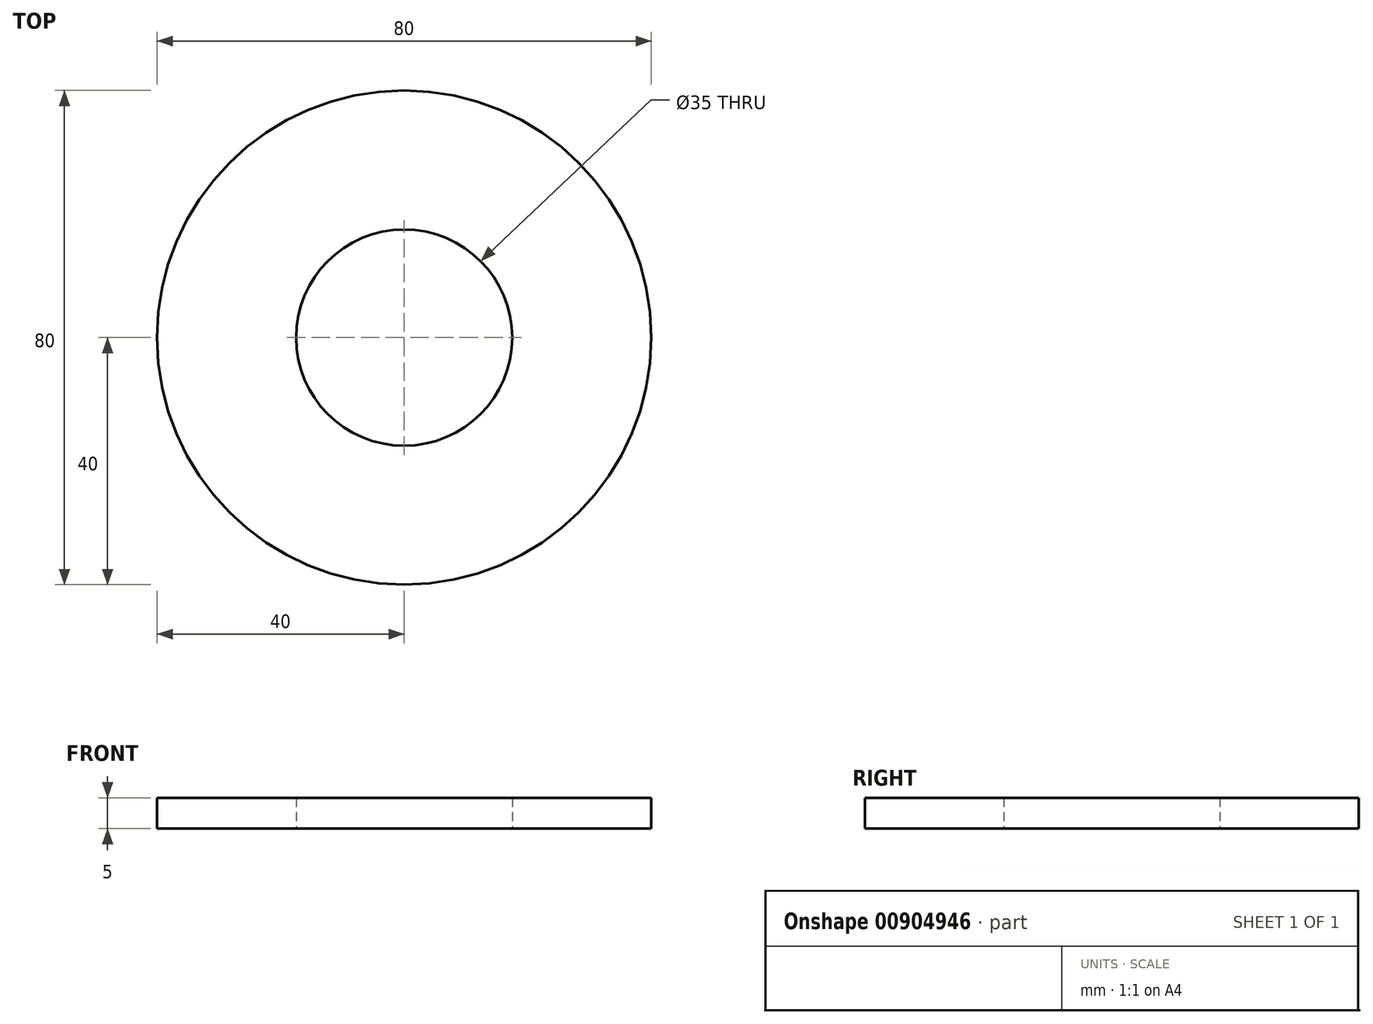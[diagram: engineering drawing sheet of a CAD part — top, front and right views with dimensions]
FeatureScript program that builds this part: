
annotation { "Feature Type Name" : "Feature", "Feature Type Description" : "" }
export const myFeature = defineFeature(function(context is Context, id is Id, definition is map)
    precondition{}
    {
        {
            var Q0;
            Q0=qCreatedBy(makeId("Top.planeOp"),FACE);
            var sketch = newSketch(context, id + "F0", { "sketchPlane" : qUnion([Q0])});
            skArc(sketch, "E0", {"start": v(9.54, 136.41) * mm, "mid": v(4.77, 136.66) * mm, "end": v(0, 136.75) * mm});
            skArc(sketch, "E1", {"start": v(8, 114.55) * mm, "mid": v(4, 114.76) * mm, "end": v(0, 114.83) * mm});
            skLineSegment(sketch, "E2", {"start": v(0, 0) * mm, "end": v(0, 38.61) * mm, "construction": true});
            skLineSegment(sketch, "E3", {"start": v(0, 10) * mm, "end": v(0, 0) * mm, "construction": true});
            skLineSegment(sketch, "E4", {"start": v(0, 0) * mm, "end": v(-47.77, 0) * mm, "construction": true});
            skLineSegment(sketch, "E5", {"start": v(0, 114.83) * mm, "end": v(0, 136.75) * mm});
            skLineSegment(sketch, "E6", {"start": v(8, 114.55) * mm, "end": v(9.54, 136.41) * mm});
            skArc(sketch, "E7.1.0", {"start": v(-10, 114.4) * mm, "mid": v(-14, 113.98) * mm, "end": v(-17.96, 113.42) * mm});
            skLineSegment(sketch, "E7.1.1", {"start": v(-17.96, 113.42) * mm, "end": v(-21.4, 135.06) * mm});
            skArc(sketch, "E7.1.2", {"start": v(-11.92, 136.23) * mm, "mid": v(-16.67, 135.73) * mm, "end": v(-21.4, 135.06) * mm});
            skLineSegment(sketch, "E7.1.3", {"start": v(-10, 114.4) * mm, "end": v(-11.92, 136.23) * mm});
            skArc(sketch, "E7.2.0", {"start": v(-27.78, 111.42) * mm, "mid": v(-31.65, 110.39) * mm, "end": v(-35.49, 109.21) * mm});
            skLineSegment(sketch, "E7.2.1", {"start": v(-35.49, 109.21) * mm, "end": v(-42.26, 130.05) * mm});
            skArc(sketch, "E7.2.2", {"start": v(-33.08, 132.68) * mm, "mid": v(-37.7, 131.45) * mm, "end": v(-42.26, 130.05) * mm});
            skLineSegment(sketch, "E7.2.3", {"start": v(-27.78, 111.42) * mm, "end": v(-33.08, 132.68) * mm});
            skArc(sketch, "E7.3.0", {"start": v(-44.87, 105.7) * mm, "mid": v(-48.53, 104.07) * mm, "end": v(-52.13, 102.32) * mm});
            skLineSegment(sketch, "E7.3.1", {"start": v(-52.13, 102.32) * mm, "end": v(-62.08, 121.84) * mm});
            skArc(sketch, "E7.3.2", {"start": v(-53.43, 125.88) * mm, "mid": v(-57.8, 123.93) * mm, "end": v(-62.08, 121.84) * mm});
            skLineSegment(sketch, "E7.3.3", {"start": v(-44.87, 105.7) * mm, "end": v(-53.43, 125.88) * mm});
            skArc(sketch, "E7.4.0", {"start": v(-60.85, 97.38) * mm, "mid": v(-64.21, 95.2) * mm, "end": v(-67.5, 92.9) * mm});
            skLineSegment(sketch, "E7.4.1", {"start": v(-67.5, 92.9) * mm, "end": v(-80.38, 110.63) * mm});
            skArc(sketch, "E7.4.2", {"start": v(-72.47, 115.97) * mm, "mid": v(-76.47, 113.37) * mm, "end": v(-80.38, 110.63) * mm});
            skLineSegment(sketch, "E7.4.3", {"start": v(-60.85, 97.38) * mm, "end": v(-72.47, 115.97) * mm});
            skArc(sketch, "E7.5.0", {"start": v(-75.34, 86.67) * mm, "mid": v(-78.32, 83.98) * mm, "end": v(-81.2, 81.2) * mm});
            skLineSegment(sketch, "E7.5.1", {"start": v(-81.2, 81.2) * mm, "end": v(-96.7, 96.7) * mm});
            skArc(sketch, "E7.5.2", {"start": v(-89.71, 103.2) * mm, "mid": v(-93.26, 100.01) * mm, "end": v(-96.7, 96.7) * mm});
            skLineSegment(sketch, "E7.5.3", {"start": v(-75.34, 86.67) * mm, "end": v(-89.71, 103.2) * mm});
            skArc(sketch, "E7.6.0", {"start": v(-87.97, 73.81) * mm, "mid": v(-90.5, 70.7) * mm, "end": v(-92.9, 67.5) * mm});
            skLineSegment(sketch, "E7.6.1", {"start": v(-92.9, 67.5) * mm, "end": v(-110.63, 80.38) * mm});
            skArc(sketch, "E7.6.2", {"start": v(-104.75, 87.9) * mm, "mid": v(-107.76, 84.19) * mm, "end": v(-110.63, 80.38) * mm});
            skLineSegment(sketch, "E7.6.3", {"start": v(-87.97, 73.81) * mm, "end": v(-104.75, 87.9) * mm});
            skArc(sketch, "E7.7.0", {"start": v(-98.43, 59.14) * mm, "mid": v(-100.44, 55.67) * mm, "end": v(-102.32, 52.13) * mm});
            skLineSegment(sketch, "E7.7.1", {"start": v(-102.32, 52.13) * mm, "end": v(-121.84, 62.08) * mm});
            skArc(sketch, "E7.7.2", {"start": v(-117.22, 70.43) * mm, "mid": v(-119.6, 66.3) * mm, "end": v(-121.84, 62.08) * mm});
            skLineSegment(sketch, "E7.7.3", {"start": v(-98.43, 59.14) * mm, "end": v(-117.22, 70.43) * mm});
            skArc(sketch, "E7.8.0", {"start": v(-106.47, 43.02) * mm, "mid": v(-107.9, 39.28) * mm, "end": v(-109.21, 35.49) * mm});
            skLineSegment(sketch, "E7.8.1", {"start": v(-109.21, 35.49) * mm, "end": v(-130.05, 42.26) * mm});
            skArc(sketch, "E7.8.2", {"start": v(-126.79, 51.23) * mm, "mid": v(-128.5, 46.77) * mm, "end": v(-130.05, 42.26) * mm});
            skLineSegment(sketch, "E7.8.3", {"start": v(-106.47, 43.02) * mm, "end": v(-126.79, 51.23) * mm});
            skArc(sketch, "E7.9.0", {"start": v(-111.9, 25.83) * mm, "mid": v(-112.72, 21.91) * mm, "end": v(-113.42, 17.96) * mm});
            skLineSegment(sketch, "E7.9.1", {"start": v(-113.42, 17.96) * mm, "end": v(-135.06, 21.4) * mm});
            skArc(sketch, "E7.9.2", {"start": v(-133.24, 30.76) * mm, "mid": v(-134.23, 26.1) * mm, "end": v(-135.06, 21.4) * mm});
            skLineSegment(sketch, "E7.9.3", {"start": v(-111.9, 25.83) * mm, "end": v(-133.24, 30.76) * mm});
            skArc(sketch, "E7.10.0", {"start": v(-114.55, 8) * mm, "mid": v(-114.76, 4) * mm, "end": v(-114.83, 0) * mm});
            skLineSegment(sketch, "E7.10.1", {"start": v(-114.83, 0) * mm, "end": v(-136.75, 0) * mm});
            skArc(sketch, "E7.10.2", {"start": v(-136.41, 9.54) * mm, "mid": v(-136.66, 4.77) * mm, "end": v(-136.75, 0) * mm});
            skLineSegment(sketch, "E7.10.3", {"start": v(-114.55, 8) * mm, "end": v(-136.41, 9.54) * mm});
            skArc(sketch, "E7.11.0", {"start": v(-114.4, -10) * mm, "mid": v(-113.98, -14) * mm, "end": v(-113.42, -17.96) * mm});
            skLineSegment(sketch, "E7.11.1", {"start": v(-113.42, -17.96) * mm, "end": v(-135.06, -21.4) * mm});
            skArc(sketch, "E7.11.2", {"start": v(-136.23, -11.92) * mm, "mid": v(-135.73, -16.67) * mm, "end": v(-135.06, -21.4) * mm});
            skLineSegment(sketch, "E7.11.3", {"start": v(-114.4, -10) * mm, "end": v(-136.23, -11.92) * mm});
            skArc(sketch, "E7.12.0", {"start": v(-111.42, -27.78) * mm, "mid": v(-110.39, -31.65) * mm, "end": v(-109.21, -35.49) * mm});
            skLineSegment(sketch, "E7.12.1", {"start": v(-109.21, -35.49) * mm, "end": v(-130.05, -42.26) * mm});
            skArc(sketch, "E7.12.2", {"start": v(-132.68, -33.08) * mm, "mid": v(-131.45, -37.7) * mm, "end": v(-130.05, -42.26) * mm});
            skLineSegment(sketch, "E7.12.3", {"start": v(-111.42, -27.78) * mm, "end": v(-132.68, -33.08) * mm});
            skArc(sketch, "E7.13.0", {"start": v(-105.7, -44.87) * mm, "mid": v(-104.07, -48.53) * mm, "end": v(-102.32, -52.13) * mm});
            skLineSegment(sketch, "E7.13.1", {"start": v(-102.32, -52.13) * mm, "end": v(-121.84, -62.08) * mm});
            skArc(sketch, "E7.13.2", {"start": v(-125.88, -53.43) * mm, "mid": v(-123.93, -57.8) * mm, "end": v(-121.84, -62.08) * mm});
            skLineSegment(sketch, "E7.13.3", {"start": v(-105.7, -44.87) * mm, "end": v(-125.88, -53.43) * mm});
            skArc(sketch, "E7.14.0", {"start": v(-97.38, -60.85) * mm, "mid": v(-95.2, -64.21) * mm, "end": v(-92.9, -67.5) * mm});
            skLineSegment(sketch, "E7.14.1", {"start": v(-92.9, -67.5) * mm, "end": v(-110.63, -80.38) * mm});
            skArc(sketch, "E7.14.2", {"start": v(-115.97, -72.47) * mm, "mid": v(-113.37, -76.47) * mm, "end": v(-110.63, -80.38) * mm});
            skLineSegment(sketch, "E7.14.3", {"start": v(-97.38, -60.85) * mm, "end": v(-115.97, -72.47) * mm});
            skArc(sketch, "E7.15.0", {"start": v(-86.67, -75.34) * mm, "mid": v(-83.98, -78.32) * mm, "end": v(-81.2, -81.2) * mm});
            skLineSegment(sketch, "E7.15.1", {"start": v(-81.2, -81.2) * mm, "end": v(-96.7, -96.7) * mm});
            skArc(sketch, "E7.15.2", {"start": v(-103.2, -89.71) * mm, "mid": v(-100.01, -93.26) * mm, "end": v(-96.7, -96.7) * mm});
            skLineSegment(sketch, "E7.15.3", {"start": v(-86.67, -75.34) * mm, "end": v(-103.2, -89.71) * mm});
            skArc(sketch, "E7.16.0", {"start": v(-73.81, -87.97) * mm, "mid": v(-70.7, -90.5) * mm, "end": v(-67.5, -92.9) * mm});
            skLineSegment(sketch, "E7.16.1", {"start": v(-67.5, -92.9) * mm, "end": v(-80.38, -110.63) * mm});
            skArc(sketch, "E7.16.2", {"start": v(-87.9, -104.75) * mm, "mid": v(-84.19, -107.76) * mm, "end": v(-80.38, -110.63) * mm});
            skLineSegment(sketch, "E7.16.3", {"start": v(-73.81, -87.97) * mm, "end": v(-87.9, -104.75) * mm});
            skArc(sketch, "E7.17.0", {"start": v(-59.14, -98.43) * mm, "mid": v(-55.67, -100.44) * mm, "end": v(-52.13, -102.32) * mm});
            skLineSegment(sketch, "E7.17.1", {"start": v(-52.13, -102.32) * mm, "end": v(-62.08, -121.84) * mm});
            skArc(sketch, "E7.17.2", {"start": v(-70.43, -117.22) * mm, "mid": v(-66.3, -119.6) * mm, "end": v(-62.08, -121.84) * mm});
            skLineSegment(sketch, "E7.17.3", {"start": v(-59.14, -98.43) * mm, "end": v(-70.43, -117.22) * mm});
            skArc(sketch, "E7.18.0", {"start": v(-43.02, -106.47) * mm, "mid": v(-39.28, -107.9) * mm, "end": v(-35.49, -109.21) * mm});
            skLineSegment(sketch, "E7.18.1", {"start": v(-35.49, -109.21) * mm, "end": v(-42.26, -130.05) * mm});
            skArc(sketch, "E7.18.2", {"start": v(-51.23, -126.79) * mm, "mid": v(-46.77, -128.5) * mm, "end": v(-42.26, -130.05) * mm});
            skLineSegment(sketch, "E7.18.3", {"start": v(-43.02, -106.47) * mm, "end": v(-51.23, -126.79) * mm});
            skArc(sketch, "E7.19.0", {"start": v(-25.83, -111.9) * mm, "mid": v(-21.91, -112.72) * mm, "end": v(-17.96, -113.42) * mm});
            skLineSegment(sketch, "E7.19.1", {"start": v(-17.96, -113.42) * mm, "end": v(-21.4, -135.06) * mm});
            skArc(sketch, "E7.19.2", {"start": v(-30.76, -133.24) * mm, "mid": v(-26.1, -134.23) * mm, "end": v(-21.4, -135.06) * mm});
            skLineSegment(sketch, "E7.19.3", {"start": v(-25.83, -111.9) * mm, "end": v(-30.76, -133.24) * mm});
            skArc(sketch, "E7.20.0", {"start": v(-8, -114.55) * mm, "mid": v(-4, -114.76) * mm, "end": v(0, -114.83) * mm});
            skLineSegment(sketch, "E7.20.1", {"start": v(0, -114.83) * mm, "end": v(0, -136.75) * mm});
            skArc(sketch, "E7.20.2", {"start": v(-9.54, -136.41) * mm, "mid": v(-4.77, -136.66) * mm, "end": v(0, -136.75) * mm});
            skLineSegment(sketch, "E7.20.3", {"start": v(-8, -114.55) * mm, "end": v(-9.54, -136.41) * mm});
            skArc(sketch, "E7.21.0", {"start": v(10, -114.4) * mm, "mid": v(14, -113.98) * mm, "end": v(17.96, -113.42) * mm});
            skLineSegment(sketch, "E7.21.1", {"start": v(17.96, -113.42) * mm, "end": v(21.4, -135.06) * mm});
            skArc(sketch, "E7.21.2", {"start": v(11.92, -136.23) * mm, "mid": v(16.67, -135.73) * mm, "end": v(21.4, -135.06) * mm});
            skLineSegment(sketch, "E7.21.3", {"start": v(10, -114.4) * mm, "end": v(11.92, -136.23) * mm});
            skArc(sketch, "E7.22.0", {"start": v(27.78, -111.42) * mm, "mid": v(31.65, -110.39) * mm, "end": v(35.49, -109.21) * mm});
            skLineSegment(sketch, "E7.22.1", {"start": v(35.49, -109.21) * mm, "end": v(42.26, -130.05) * mm});
            skArc(sketch, "E7.22.2", {"start": v(33.08, -132.68) * mm, "mid": v(37.7, -131.45) * mm, "end": v(42.26, -130.05) * mm});
            skLineSegment(sketch, "E7.22.3", {"start": v(27.78, -111.42) * mm, "end": v(33.08, -132.68) * mm});
            skArc(sketch, "E7.23.0", {"start": v(44.87, -105.7) * mm, "mid": v(48.53, -104.07) * mm, "end": v(52.13, -102.32) * mm});
            skLineSegment(sketch, "E7.23.1", {"start": v(52.13, -102.32) * mm, "end": v(62.08, -121.84) * mm});
            skArc(sketch, "E7.23.2", {"start": v(53.43, -125.88) * mm, "mid": v(57.8, -123.93) * mm, "end": v(62.08, -121.84) * mm});
            skLineSegment(sketch, "E7.23.3", {"start": v(44.87, -105.7) * mm, "end": v(53.43, -125.88) * mm});
            skArc(sketch, "E7.24.0", {"start": v(60.85, -97.38) * mm, "mid": v(64.21, -95.2) * mm, "end": v(67.5, -92.9) * mm});
            skLineSegment(sketch, "E7.24.1", {"start": v(67.5, -92.9) * mm, "end": v(80.38, -110.63) * mm});
            skArc(sketch, "E7.24.2", {"start": v(72.47, -115.97) * mm, "mid": v(76.47, -113.37) * mm, "end": v(80.38, -110.63) * mm});
            skLineSegment(sketch, "E7.24.3", {"start": v(60.85, -97.38) * mm, "end": v(72.47, -115.97) * mm});
            skArc(sketch, "E7.25.0", {"start": v(75.34, -86.67) * mm, "mid": v(78.32, -83.98) * mm, "end": v(81.2, -81.2) * mm});
            skLineSegment(sketch, "E7.25.1", {"start": v(81.2, -81.2) * mm, "end": v(96.7, -96.7) * mm});
            skArc(sketch, "E7.25.2", {"start": v(89.71, -103.2) * mm, "mid": v(93.26, -100.01) * mm, "end": v(96.7, -96.7) * mm});
            skLineSegment(sketch, "E7.25.3", {"start": v(75.34, -86.67) * mm, "end": v(89.71, -103.2) * mm});
            skArc(sketch, "E7.26.0", {"start": v(87.97, -73.81) * mm, "mid": v(90.5, -70.7) * mm, "end": v(92.9, -67.5) * mm});
            skLineSegment(sketch, "E7.26.1", {"start": v(92.9, -67.5) * mm, "end": v(110.63, -80.38) * mm});
            skArc(sketch, "E7.26.2", {"start": v(104.75, -87.9) * mm, "mid": v(107.76, -84.19) * mm, "end": v(110.63, -80.38) * mm});
            skLineSegment(sketch, "E7.26.3", {"start": v(87.97, -73.81) * mm, "end": v(104.75, -87.9) * mm});
            skArc(sketch, "E7.27.0", {"start": v(98.43, -59.14) * mm, "mid": v(100.44, -55.67) * mm, "end": v(102.32, -52.13) * mm});
            skLineSegment(sketch, "E7.27.1", {"start": v(102.32, -52.13) * mm, "end": v(121.84, -62.08) * mm});
            skArc(sketch, "E7.27.2", {"start": v(117.22, -70.43) * mm, "mid": v(119.6, -66.3) * mm, "end": v(121.84, -62.08) * mm});
            skLineSegment(sketch, "E7.27.3", {"start": v(98.43, -59.14) * mm, "end": v(117.22, -70.43) * mm});
            skArc(sketch, "E7.28.0", {"start": v(106.47, -43.02) * mm, "mid": v(107.9, -39.28) * mm, "end": v(109.21, -35.49) * mm});
            skLineSegment(sketch, "E7.28.1", {"start": v(109.21, -35.49) * mm, "end": v(130.05, -42.26) * mm});
            skArc(sketch, "E7.28.2", {"start": v(126.79, -51.23) * mm, "mid": v(128.5, -46.77) * mm, "end": v(130.05, -42.26) * mm});
            skLineSegment(sketch, "E7.28.3", {"start": v(106.47, -43.02) * mm, "end": v(126.79, -51.23) * mm});
            skArc(sketch, "E7.29.0", {"start": v(111.9, -25.83) * mm, "mid": v(112.72, -21.91) * mm, "end": v(113.42, -17.96) * mm});
            skLineSegment(sketch, "E7.29.1", {"start": v(113.42, -17.96) * mm, "end": v(135.06, -21.4) * mm});
            skArc(sketch, "E7.29.2", {"start": v(133.24, -30.76) * mm, "mid": v(134.23, -26.1) * mm, "end": v(135.06, -21.4) * mm});
            skLineSegment(sketch, "E7.29.3", {"start": v(111.9, -25.83) * mm, "end": v(133.24, -30.76) * mm});
            skArc(sketch, "E7.30.0", {"start": v(114.55, -8) * mm, "mid": v(114.76, -4) * mm, "end": v(114.83, 0) * mm});
            skLineSegment(sketch, "E7.30.1", {"start": v(114.83, 0) * mm, "end": v(136.75, 0) * mm});
            skArc(sketch, "E7.30.2", {"start": v(136.41, -9.54) * mm, "mid": v(136.66, -4.77) * mm, "end": v(136.75, 0) * mm});
            skLineSegment(sketch, "E7.30.3", {"start": v(114.55, -8) * mm, "end": v(136.41, -9.54) * mm});
            skArc(sketch, "E7.31.0", {"start": v(114.4, 10) * mm, "mid": v(113.98, 14) * mm, "end": v(113.42, 17.96) * mm});
            skLineSegment(sketch, "E7.31.1", {"start": v(113.42, 17.96) * mm, "end": v(135.06, 21.4) * mm});
            skArc(sketch, "E7.31.2", {"start": v(136.23, 11.92) * mm, "mid": v(135.73, 16.67) * mm, "end": v(135.06, 21.4) * mm});
            skLineSegment(sketch, "E7.31.3", {"start": v(114.4, 10) * mm, "end": v(136.23, 11.92) * mm});
            skArc(sketch, "E7.32.0", {"start": v(111.42, 27.78) * mm, "mid": v(110.39, 31.65) * mm, "end": v(109.21, 35.49) * mm});
            skLineSegment(sketch, "E7.32.1", {"start": v(109.21, 35.49) * mm, "end": v(130.05, 42.26) * mm});
            skArc(sketch, "E7.32.2", {"start": v(132.68, 33.08) * mm, "mid": v(131.45, 37.7) * mm, "end": v(130.05, 42.26) * mm});
            skLineSegment(sketch, "E7.32.3", {"start": v(111.42, 27.78) * mm, "end": v(132.68, 33.08) * mm});
            skArc(sketch, "E7.33.0", {"start": v(105.7, 44.87) * mm, "mid": v(104.07, 48.53) * mm, "end": v(102.32, 52.13) * mm});
            skLineSegment(sketch, "E7.33.1", {"start": v(102.32, 52.13) * mm, "end": v(121.84, 62.08) * mm});
            skArc(sketch, "E7.33.2", {"start": v(125.88, 53.43) * mm, "mid": v(123.93, 57.8) * mm, "end": v(121.84, 62.08) * mm});
            skLineSegment(sketch, "E7.33.3", {"start": v(105.7, 44.87) * mm, "end": v(125.88, 53.43) * mm});
            skArc(sketch, "E7.34.0", {"start": v(97.38, 60.85) * mm, "mid": v(95.2, 64.21) * mm, "end": v(92.9, 67.5) * mm});
            skLineSegment(sketch, "E7.34.1", {"start": v(92.9, 67.5) * mm, "end": v(110.63, 80.38) * mm});
            skArc(sketch, "E7.34.2", {"start": v(115.97, 72.47) * mm, "mid": v(113.37, 76.47) * mm, "end": v(110.63, 80.38) * mm});
            skLineSegment(sketch, "E7.34.3", {"start": v(97.38, 60.85) * mm, "end": v(115.97, 72.47) * mm});
            skArc(sketch, "E7.35.0", {"start": v(86.67, 75.34) * mm, "mid": v(83.98, 78.32) * mm, "end": v(81.2, 81.2) * mm});
            skLineSegment(sketch, "E7.35.1", {"start": v(81.2, 81.2) * mm, "end": v(96.7, 96.7) * mm});
            skArc(sketch, "E7.35.2", {"start": v(103.2, 89.71) * mm, "mid": v(100.01, 93.26) * mm, "end": v(96.7, 96.7) * mm});
            skLineSegment(sketch, "E7.35.3", {"start": v(86.67, 75.34) * mm, "end": v(103.2, 89.71) * mm});
            skArc(sketch, "E7.36.0", {"start": v(73.81, 87.97) * mm, "mid": v(70.7, 90.5) * mm, "end": v(67.5, 92.9) * mm});
            skLineSegment(sketch, "E7.36.1", {"start": v(67.5, 92.9) * mm, "end": v(80.38, 110.63) * mm});
            skArc(sketch, "E7.36.2", {"start": v(87.9, 104.75) * mm, "mid": v(84.19, 107.76) * mm, "end": v(80.38, 110.63) * mm});
            skLineSegment(sketch, "E7.36.3", {"start": v(73.81, 87.97) * mm, "end": v(87.9, 104.75) * mm});
            skArc(sketch, "E7.37.0", {"start": v(59.14, 98.43) * mm, "mid": v(55.67, 100.44) * mm, "end": v(52.13, 102.32) * mm});
            skLineSegment(sketch, "E7.37.1", {"start": v(52.13, 102.32) * mm, "end": v(62.08, 121.84) * mm});
            skArc(sketch, "E7.37.2", {"start": v(70.43, 117.22) * mm, "mid": v(66.3, 119.6) * mm, "end": v(62.08, 121.84) * mm});
            skLineSegment(sketch, "E7.37.3", {"start": v(59.14, 98.43) * mm, "end": v(70.43, 117.22) * mm});
            skArc(sketch, "E7.38.0", {"start": v(43.02, 106.47) * mm, "mid": v(39.28, 107.9) * mm, "end": v(35.49, 109.21) * mm});
            skLineSegment(sketch, "E7.38.1", {"start": v(35.49, 109.21) * mm, "end": v(42.26, 130.05) * mm});
            skArc(sketch, "E7.38.2", {"start": v(51.23, 126.79) * mm, "mid": v(46.77, 128.5) * mm, "end": v(42.26, 130.05) * mm});
            skLineSegment(sketch, "E7.38.3", {"start": v(43.02, 106.47) * mm, "end": v(51.23, 126.79) * mm});
            skArc(sketch, "E7.39.0", {"start": v(25.83, 111.9) * mm, "mid": v(21.91, 112.72) * mm, "end": v(17.96, 113.42) * mm});
            skLineSegment(sketch, "E7.39.1", {"start": v(17.96, 113.42) * mm, "end": v(21.4, 135.06) * mm});
            skArc(sketch, "E7.39.2", {"start": v(30.76, 133.24) * mm, "mid": v(26.1, 134.23) * mm, "end": v(21.4, 135.06) * mm});
            skLineSegment(sketch, "E7.39.3", {"start": v(25.83, 111.9) * mm, "end": v(30.76, 133.24) * mm});
            skCircle(sketch, "E8", {"center": v(0, 0) * mm, "radius": 290 * mm});
            skArc(sketch, "E9", {"start": v(40.17, 195.92) * mm, "mid": v(20.2, 198.98) * mm, "end": v(0, 200) * mm});
            skArc(sketch, "E10", {"start": v(60.9, 273.3) * mm, "mid": v(30.64, 278.32) * mm, "end": v(0, 280) * mm});
            skLineSegment(sketch, "E11", {"start": v(0, 0) * mm, "end": v(0, 38.61) * mm});
            skLineSegment(sketch, "E12.trimOffspring", {"start": v(0, 200) * mm, "end": v(0, 280) * mm});
            skLineSegment(sketch, "E13.trimOffspring", {"start": v(40.17, 195.92) * mm, "end": v(60.9, 273.3) * mm});
            skLineSegment(sketch, "E14.trimOffspring", {"start": v(0, 114.83) * mm, "end": v(0, 145) * mm});
            skArc(sketch, "E15.1.0", {"start": v(-63.17, 189.76) * mm, "mid": v(-82, 182.42) * mm, "end": v(-100, 173.2) * mm});
            skLineSegment(sketch, "E15.1.1", {"start": v(-100, 173.2) * mm, "end": v(-140, 242.49) * mm});
            skArc(sketch, "E15.1.2", {"start": v(-83.9, 267.13) * mm, "mid": v(-112.63, 256.35) * mm, "end": v(-140, 242.49) * mm});
            skLineSegment(sketch, "E15.1.3", {"start": v(-63.17, 189.76) * mm, "end": v(-83.9, 267.13) * mm});
            skArc(sketch, "E15.2.0", {"start": v(-149.59, 132.75) * mm, "mid": v(-162.23, 116.97) * mm, "end": v(-173.2, 100) * mm});
            skLineSegment(sketch, "E15.2.1", {"start": v(-173.2, 100) * mm, "end": v(-242.49, 140) * mm});
            skArc(sketch, "E15.2.2", {"start": v(-206.23, 189.4) * mm, "mid": v(-225.71, 165.7) * mm, "end": v(-242.49, 140) * mm});
            skLineSegment(sketch, "E15.2.3", {"start": v(-149.59, 132.75) * mm, "end": v(-206.23, 189.4) * mm});
            skArc(sketch, "E15.3.0", {"start": v(-195.92, 40.17) * mm, "mid": v(-198.98, 20.2) * mm, "end": v(-200, 0) * mm});
            skLineSegment(sketch, "E15.3.1", {"start": v(-200, 0) * mm, "end": v(-280, 0) * mm});
            skArc(sketch, "E15.3.2", {"start": v(-273.3, 60.9) * mm, "mid": v(-278.32, 30.64) * mm, "end": v(-280, 0) * mm});
            skLineSegment(sketch, "E15.3.3", {"start": v(-195.92, 40.17) * mm, "end": v(-273.3, 60.9) * mm});
            skArc(sketch, "E15.4.0", {"start": v(-189.76, -63.17) * mm, "mid": v(-182.42, -82) * mm, "end": v(-173.2, -100) * mm});
            skLineSegment(sketch, "E15.4.1", {"start": v(-173.2, -100) * mm, "end": v(-242.49, -140) * mm});
            skArc(sketch, "E15.4.2", {"start": v(-267.13, -83.9) * mm, "mid": v(-256.35, -112.63) * mm, "end": v(-242.49, -140) * mm});
            skLineSegment(sketch, "E15.4.3", {"start": v(-189.76, -63.17) * mm, "end": v(-267.13, -83.9) * mm});
            skArc(sketch, "E15.5.0", {"start": v(-132.75, -149.59) * mm, "mid": v(-116.97, -162.23) * mm, "end": v(-100, -173.2) * mm});
            skLineSegment(sketch, "E15.5.1", {"start": v(-100, -173.2) * mm, "end": v(-140, -242.49) * mm});
            skArc(sketch, "E15.5.2", {"start": v(-189.4, -206.23) * mm, "mid": v(-165.7, -225.71) * mm, "end": v(-140, -242.49) * mm});
            skLineSegment(sketch, "E15.5.3", {"start": v(-132.75, -149.59) * mm, "end": v(-189.4, -206.23) * mm});
            skArc(sketch, "E15.6.0", {"start": v(-40.17, -195.92) * mm, "mid": v(-20.2, -198.98) * mm, "end": v(0, -200) * mm});
            skLineSegment(sketch, "E15.6.1", {"start": v(0, -200) * mm, "end": v(0, -280) * mm});
            skArc(sketch, "E15.6.2", {"start": v(-60.9, -273.3) * mm, "mid": v(-30.64, -278.32) * mm, "end": v(0, -280) * mm});
            skLineSegment(sketch, "E15.6.3", {"start": v(-40.17, -195.92) * mm, "end": v(-60.9, -273.3) * mm});
            skArc(sketch, "E15.7.0", {"start": v(63.17, -189.76) * mm, "mid": v(82, -182.42) * mm, "end": v(100, -173.2) * mm});
            skLineSegment(sketch, "E15.7.1", {"start": v(100, -173.2) * mm, "end": v(140, -242.49) * mm});
            skArc(sketch, "E15.7.2", {"start": v(83.9, -267.13) * mm, "mid": v(112.63, -256.35) * mm, "end": v(140, -242.49) * mm});
            skLineSegment(sketch, "E15.7.3", {"start": v(63.17, -189.76) * mm, "end": v(83.9, -267.13) * mm});
            skArc(sketch, "E15.8.0", {"start": v(149.59, -132.75) * mm, "mid": v(162.23, -116.97) * mm, "end": v(173.2, -100) * mm});
            skLineSegment(sketch, "E15.8.1", {"start": v(173.2, -100) * mm, "end": v(242.49, -140) * mm});
            skArc(sketch, "E15.8.2", {"start": v(206.23, -189.4) * mm, "mid": v(225.71, -165.7) * mm, "end": v(242.49, -140) * mm});
            skLineSegment(sketch, "E15.8.3", {"start": v(149.59, -132.75) * mm, "end": v(206.23, -189.4) * mm});
            skArc(sketch, "E15.9.0", {"start": v(195.92, -40.17) * mm, "mid": v(198.98, -20.2) * mm, "end": v(200, 0) * mm});
            skLineSegment(sketch, "E15.9.1", {"start": v(200, 0) * mm, "end": v(280, 0) * mm});
            skArc(sketch, "E15.9.2", {"start": v(273.3, -60.9) * mm, "mid": v(278.32, -30.64) * mm, "end": v(280, 0) * mm});
            skLineSegment(sketch, "E15.9.3", {"start": v(195.92, -40.17) * mm, "end": v(273.3, -60.9) * mm});
            skArc(sketch, "E15.10.0", {"start": v(189.76, 63.17) * mm, "mid": v(182.42, 82) * mm, "end": v(173.2, 100) * mm});
            skLineSegment(sketch, "E15.10.1", {"start": v(173.2, 100) * mm, "end": v(242.49, 140) * mm});
            skArc(sketch, "E15.10.2", {"start": v(267.13, 83.9) * mm, "mid": v(256.35, 112.63) * mm, "end": v(242.49, 140) * mm});
            skLineSegment(sketch, "E15.10.3", {"start": v(189.76, 63.17) * mm, "end": v(267.13, 83.9) * mm});
            skArc(sketch, "E15.11.0", {"start": v(132.75, 149.59) * mm, "mid": v(116.97, 162.23) * mm, "end": v(100, 173.2) * mm});
            skLineSegment(sketch, "E15.11.1", {"start": v(100, 173.2) * mm, "end": v(140, 242.49) * mm});
            skArc(sketch, "E15.11.2", {"start": v(189.4, 206.23) * mm, "mid": v(165.7, 225.71) * mm, "end": v(140, 242.49) * mm});
            skLineSegment(sketch, "E15.11.3", {"start": v(132.75, 149.59) * mm, "end": v(189.4, 206.23) * mm});
            skLineSegment(sketch, "E16.bottom", {"start": v(5, -5) * mm, "end": v(-5, -5) * mm});
            skLineSegment(sketch, "E16.top", {"start": v(5, 5) * mm, "end": v(-5, 5) * mm});
            skLineSegment(sketch, "E16.left", {"start": v(5, -5) * mm, "end": v(5, 5) * mm});
            skLineSegment(sketch, "E16.right", {"start": v(-5, -5) * mm, "end": v(-5, 5) * mm});
            skSolve(sketch);
        }
        {
            var Q0;
            Q0=qSketchRegion(id+"F0",true);
            extrude(context, id + "F1", {"entities" : qUnion([Q0]), "depth" : 5 * mm, "offsetDistance" : 25 * mm});
        }
        {
            var Q0;
            Q0=makeQuery(id+"F1.opExtrude","CAP_FACE",FACE,{"disambiguationData":[OSD([sQuery(id+"F0.wireOp",EDGE,"E0"),sQuery(id+"F0.wireOp",EDGE,"E1"),sQuery(id+"F0.wireOp",EDGE,"E6"),sQuery(id+"F0.wireOp",EDGE,"E7.1.0"),sQuery(id+"F0.wireOp",EDGE,"E7.1.1"),sQuery(id+"F0.wireOp",EDGE,"E7.1.2"),sQuery(id+"F0.wireOp",EDGE,"E7.1.3"),sQuery(id+"F0.wireOp",EDGE,"E7.2.0"),sQuery(id+"F0.wireOp",EDGE,"E7.2.1"),sQuery(id+"F0.wireOp",EDGE,"E7.2.2"),sQuery(id+"F0.wireOp",EDGE,"E7.2.3"),sQuery(id+"F0.wireOp",EDGE,"E7.3.0"),sQuery(id+"F0.wireOp",EDGE,"E7.3.1"),sQuery(id+"F0.wireOp",EDGE,"E7.3.2"),sQuery(id+"F0.wireOp",EDGE,"E7.3.3"),sQuery(id+"F0.wireOp",EDGE,"E7.4.0"),sQuery(id+"F0.wireOp",EDGE,"E7.4.1"),sQuery(id+"F0.wireOp",EDGE,"E7.4.2"),sQuery(id+"F0.wireOp",EDGE,"E7.4.3"),sQuery(id+"F0.wireOp",EDGE,"E7.5.0"),sQuery(id+"F0.wireOp",EDGE,"E7.5.1"),sQuery(id+"F0.wireOp",EDGE,"E7.5.2"),sQuery(id+"F0.wireOp",EDGE,"E7.5.3"),sQuery(id+"F0.wireOp",EDGE,"E7.6.0"),sQuery(id+"F0.wireOp",EDGE,"E7.6.1"),sQuery(id+"F0.wireOp",EDGE,"E7.6.2"),sQuery(id+"F0.wireOp",EDGE,"E7.6.3"),sQuery(id+"F0.wireOp",EDGE,"E7.7.0"),sQuery(id+"F0.wireOp",EDGE,"E7.7.1"),sQuery(id+"F0.wireOp",EDGE,"E7.7.2"),sQuery(id+"F0.wireOp",EDGE,"E7.7.3"),sQuery(id+"F0.wireOp",EDGE,"E7.8.0"),sQuery(id+"F0.wireOp",EDGE,"E7.8.1"),sQuery(id+"F0.wireOp",EDGE,"E7.8.2"),sQuery(id+"F0.wireOp",EDGE,"E7.8.3"),sQuery(id+"F0.wireOp",EDGE,"E7.9.0"),sQuery(id+"F0.wireOp",EDGE,"E7.9.1"),sQuery(id+"F0.wireOp",EDGE,"E7.9.2"),sQuery(id+"F0.wireOp",EDGE,"E7.9.3"),sQuery(id+"F0.wireOp",EDGE,"E7.10.0"),sQuery(id+"F0.wireOp",EDGE,"E7.10.1"),sQuery(id+"F0.wireOp",EDGE,"E7.10.2"),sQuery(id+"F0.wireOp",EDGE,"E7.10.3"),sQuery(id+"F0.wireOp",EDGE,"E7.11.0"),sQuery(id+"F0.wireOp",EDGE,"E7.11.1"),sQuery(id+"F0.wireOp",EDGE,"E7.11.2"),sQuery(id+"F0.wireOp",EDGE,"E7.11.3"),sQuery(id+"F0.wireOp",EDGE,"E7.12.0"),sQuery(id+"F0.wireOp",EDGE,"E7.12.1"),sQuery(id+"F0.wireOp",EDGE,"E7.12.2"),sQuery(id+"F0.wireOp",EDGE,"E7.12.3"),sQuery(id+"F0.wireOp",EDGE,"E7.13.0"),sQuery(id+"F0.wireOp",EDGE,"E7.13.1"),sQuery(id+"F0.wireOp",EDGE,"E7.13.2"),sQuery(id+"F0.wireOp",EDGE,"E7.13.3"),sQuery(id+"F0.wireOp",EDGE,"E7.14.0"),sQuery(id+"F0.wireOp",EDGE,"E7.14.1"),sQuery(id+"F0.wireOp",EDGE,"E7.14.2"),sQuery(id+"F0.wireOp",EDGE,"E7.14.3"),sQuery(id+"F0.wireOp",EDGE,"E7.15.0"),sQuery(id+"F0.wireOp",EDGE,"E7.15.1"),sQuery(id+"F0.wireOp",EDGE,"E7.15.2"),sQuery(id+"F0.wireOp",EDGE,"E7.15.3"),sQuery(id+"F0.wireOp",EDGE,"E7.16.0"),sQuery(id+"F0.wireOp",EDGE,"E7.16.1"),sQuery(id+"F0.wireOp",EDGE,"E7.16.2"),sQuery(id+"F0.wireOp",EDGE,"E7.16.3"),sQuery(id+"F0.wireOp",EDGE,"E7.17.0"),sQuery(id+"F0.wireOp",EDGE,"E7.17.1"),sQuery(id+"F0.wireOp",EDGE,"E7.17.2"),sQuery(id+"F0.wireOp",EDGE,"E7.17.3"),sQuery(id+"F0.wireOp",EDGE,"E7.18.0"),sQuery(id+"F0.wireOp",EDGE,"E7.18.1"),sQuery(id+"F0.wireOp",EDGE,"E7.18.2"),sQuery(id+"F0.wireOp",EDGE,"E7.18.3"),sQuery(id+"F0.wireOp",EDGE,"E7.19.0"),sQuery(id+"F0.wireOp",EDGE,"E7.19.1"),sQuery(id+"F0.wireOp",EDGE,"E7.19.2"),sQuery(id+"F0.wireOp",EDGE,"E7.19.3"),sQuery(id+"F0.wireOp",EDGE,"E7.20.0"),sQuery(id+"F0.wireOp",EDGE,"E7.20.1"),sQuery(id+"F0.wireOp",EDGE,"E7.20.2"),sQuery(id+"F0.wireOp",EDGE,"E7.20.3"),sQuery(id+"F0.wireOp",EDGE,"E7.21.0"),sQuery(id+"F0.wireOp",EDGE,"E7.21.1"),sQuery(id+"F0.wireOp",EDGE,"E7.21.2"),sQuery(id+"F0.wireOp",EDGE,"E7.21.3"),sQuery(id+"F0.wireOp",EDGE,"E7.22.0"),sQuery(id+"F0.wireOp",EDGE,"E7.22.1"),sQuery(id+"F0.wireOp",EDGE,"E7.22.2"),sQuery(id+"F0.wireOp",EDGE,"E7.22.3"),sQuery(id+"F0.wireOp",EDGE,"E7.23.0"),sQuery(id+"F0.wireOp",EDGE,"E7.23.1"),sQuery(id+"F0.wireOp",EDGE,"E7.23.2"),sQuery(id+"F0.wireOp",EDGE,"E7.23.3"),sQuery(id+"F0.wireOp",EDGE,"E7.24.0"),sQuery(id+"F0.wireOp",EDGE,"E7.24.1"),sQuery(id+"F0.wireOp",EDGE,"E7.24.2"),sQuery(id+"F0.wireOp",EDGE,"E7.24.3"),sQuery(id+"F0.wireOp",EDGE,"E7.25.0"),sQuery(id+"F0.wireOp",EDGE,"E7.25.1"),sQuery(id+"F0.wireOp",EDGE,"E7.25.2"),sQuery(id+"F0.wireOp",EDGE,"E7.25.3"),sQuery(id+"F0.wireOp",EDGE,"E7.26.0"),sQuery(id+"F0.wireOp",EDGE,"E7.26.1"),sQuery(id+"F0.wireOp",EDGE,"E7.26.2"),sQuery(id+"F0.wireOp",EDGE,"E7.26.3"),sQuery(id+"F0.wireOp",EDGE,"E7.27.0"),sQuery(id+"F0.wireOp",EDGE,"E7.27.1"),sQuery(id+"F0.wireOp",EDGE,"E7.27.2"),sQuery(id+"F0.wireOp",EDGE,"E7.27.3"),sQuery(id+"F0.wireOp",EDGE,"E7.28.0"),sQuery(id+"F0.wireOp",EDGE,"E7.28.1"),sQuery(id+"F0.wireOp",EDGE,"E7.28.2"),sQuery(id+"F0.wireOp",EDGE,"E7.28.3"),sQuery(id+"F0.wireOp",EDGE,"E7.29.0"),sQuery(id+"F0.wireOp",EDGE,"E7.29.1"),sQuery(id+"F0.wireOp",EDGE,"E7.29.2"),sQuery(id+"F0.wireOp",EDGE,"E7.29.3"),sQuery(id+"F0.wireOp",EDGE,"E7.30.0"),sQuery(id+"F0.wireOp",EDGE,"E7.30.1"),sQuery(id+"F0.wireOp",EDGE,"E7.30.2"),sQuery(id+"F0.wireOp",EDGE,"E7.30.3"),sQuery(id+"F0.wireOp",EDGE,"E7.31.0"),sQuery(id+"F0.wireOp",EDGE,"E7.31.1"),sQuery(id+"F0.wireOp",EDGE,"E7.31.2"),sQuery(id+"F0.wireOp",EDGE,"E7.31.3"),sQuery(id+"F0.wireOp",EDGE,"E7.32.0"),sQuery(id+"F0.wireOp",EDGE,"E7.32.1"),sQuery(id+"F0.wireOp",EDGE,"E7.32.2"),sQuery(id+"F0.wireOp",EDGE,"E7.32.3"),sQuery(id+"F0.wireOp",EDGE,"E7.33.0"),sQuery(id+"F0.wireOp",EDGE,"E7.33.1"),sQuery(id+"F0.wireOp",EDGE,"E7.33.2"),sQuery(id+"F0.wireOp",EDGE,"E7.33.3"),sQuery(id+"F0.wireOp",EDGE,"E7.34.0"),sQuery(id+"F0.wireOp",EDGE,"E7.34.1"),sQuery(id+"F0.wireOp",EDGE,"E7.34.2"),sQuery(id+"F0.wireOp",EDGE,"E7.34.3"),sQuery(id+"F0.wireOp",EDGE,"E7.35.0"),sQuery(id+"F0.wireOp",EDGE,"E7.35.1"),sQuery(id+"F0.wireOp",EDGE,"E7.35.2"),sQuery(id+"F0.wireOp",EDGE,"E7.35.3"),sQuery(id+"F0.wireOp",EDGE,"E7.36.0"),sQuery(id+"F0.wireOp",EDGE,"E7.36.1"),sQuery(id+"F0.wireOp",EDGE,"E7.36.2"),sQuery(id+"F0.wireOp",EDGE,"E7.36.3"),sQuery(id+"F0.wireOp",EDGE,"E7.37.0"),sQuery(id+"F0.wireOp",EDGE,"E7.37.1"),sQuery(id+"F0.wireOp",EDGE,"E7.37.2"),sQuery(id+"F0.wireOp",EDGE,"E7.37.3"),sQuery(id+"F0.wireOp",EDGE,"E7.38.0"),sQuery(id+"F0.wireOp",EDGE,"E7.38.1"),sQuery(id+"F0.wireOp",EDGE,"E7.38.2"),sQuery(id+"F0.wireOp",EDGE,"E7.38.3"),sQuery(id+"F0.wireOp",EDGE,"E7.39.0"),sQuery(id+"F0.wireOp",EDGE,"E7.39.1"),sQuery(id+"F0.wireOp",EDGE,"E7.39.2"),sQuery(id+"F0.wireOp",EDGE,"E7.39.3"),sQuery(id+"F0.wireOp",EDGE,"E8"),sQuery(id+"F0.wireOp",EDGE,"E9"),sQuery(id+"F0.wireOp",EDGE,"E10"),sQuery(id+"F0.wireOp",EDGE,"E12.trimOffspring"),sQuery(id+"F0.wireOp",EDGE,"E13.trimOffspring"),sQuery(id+"F0.wireOp",EDGE,"E14.trimOffspring"),sQuery(id+"F0.wireOp",EDGE,"E15.1.0"),sQuery(id+"F0.wireOp",EDGE,"E15.1.1"),sQuery(id+"F0.wireOp",EDGE,"E15.1.2"),sQuery(id+"F0.wireOp",EDGE,"E15.1.3"),sQuery(id+"F0.wireOp",EDGE,"E15.2.0"),sQuery(id+"F0.wireOp",EDGE,"E15.2.1"),sQuery(id+"F0.wireOp",EDGE,"E15.2.2"),sQuery(id+"F0.wireOp",EDGE,"E15.2.3"),sQuery(id+"F0.wireOp",EDGE,"E15.3.0"),sQuery(id+"F0.wireOp",EDGE,"E15.3.1"),sQuery(id+"F0.wireOp",EDGE,"E15.3.2"),sQuery(id+"F0.wireOp",EDGE,"E15.3.3"),sQuery(id+"F0.wireOp",EDGE,"E15.4.0"),sQuery(id+"F0.wireOp",EDGE,"E15.4.1"),sQuery(id+"F0.wireOp",EDGE,"E15.4.2"),sQuery(id+"F0.wireOp",EDGE,"E15.4.3"),sQuery(id+"F0.wireOp",EDGE,"E15.5.0"),sQuery(id+"F0.wireOp",EDGE,"E15.5.1"),sQuery(id+"F0.wireOp",EDGE,"E15.5.2"),sQuery(id+"F0.wireOp",EDGE,"E15.5.3"),sQuery(id+"F0.wireOp",EDGE,"E15.6.0"),sQuery(id+"F0.wireOp",EDGE,"E15.6.1"),sQuery(id+"F0.wireOp",EDGE,"E15.6.2"),sQuery(id+"F0.wireOp",EDGE,"E15.6.3"),sQuery(id+"F0.wireOp",EDGE,"E15.7.0"),sQuery(id+"F0.wireOp",EDGE,"E15.7.1"),sQuery(id+"F0.wireOp",EDGE,"E15.7.2"),sQuery(id+"F0.wireOp",EDGE,"E15.7.3"),sQuery(id+"F0.wireOp",EDGE,"E15.8.0"),sQuery(id+"F0.wireOp",EDGE,"E15.8.1"),sQuery(id+"F0.wireOp",EDGE,"E15.8.2"),sQuery(id+"F0.wireOp",EDGE,"E15.8.3"),sQuery(id+"F0.wireOp",EDGE,"E15.9.0"),sQuery(id+"F0.wireOp",EDGE,"E15.9.1"),sQuery(id+"F0.wireOp",EDGE,"E15.9.2"),sQuery(id+"F0.wireOp",EDGE,"E15.9.3"),sQuery(id+"F0.wireOp",EDGE,"E15.10.0"),sQuery(id+"F0.wireOp",EDGE,"E15.10.1"),sQuery(id+"F0.wireOp",EDGE,"E15.10.2"),sQuery(id+"F0.wireOp",EDGE,"E15.10.3"),sQuery(id+"F0.wireOp",EDGE,"E15.11.0"),sQuery(id+"F0.wireOp",EDGE,"E15.11.1"),sQuery(id+"F0.wireOp",EDGE,"E15.11.2"),sQuery(id+"F0.wireOp",EDGE,"E15.11.3"),sQuery(id+"F0.wireOp",EDGE,"E16.bottom"),sQuery(id+"F0.wireOp",EDGE,"E16.top"),sQuery(id+"F0.wireOp",EDGE,"E16.left"),sQuery(id+"F0.wireOp",EDGE,"E16.right")])],"isStart":false});
            var sketch = newSketch(context, id + "F2", { "sketchPlane" : qUnion([Q0])});
            skCircle(sketch, "E17", {"center": v(0, 0) * mm, "radius": 11 * mm});
            skSolve(sketch);
        }
        {
            var Q0;
            Q0=qSketchRegion(id+"F2",true);
            extrude(context, id + "F3", {"entities" : qUnion([Q0]), "operationType" : NewBodyOperationType.REMOVE, "oppositeDirection" : true, "depth" : 25 * mm, "offsetDistance" : 25 * mm});
        }
        {
            var Q0;
            Q0=qSketchRegion(id+"F2",true);
            extrude(context, id + "F4", {"entities" : qUnion([Q0]), "depth" : 80 * mm, "offsetDistance" : 25 * mm, "symmetric" : true});
        }
        {
            var Q0;
            Q0=makeQuery(id+"F1.opExtrude","CAP_FACE",FACE,{"disambiguationData":[OSD([sQuery(id+"F0.wireOp",EDGE,"E0"),sQuery(id+"F0.wireOp",EDGE,"E1"),sQuery(id+"F0.wireOp",EDGE,"E6"),sQuery(id+"F0.wireOp",EDGE,"E7.1.0"),sQuery(id+"F0.wireOp",EDGE,"E7.1.1"),sQuery(id+"F0.wireOp",EDGE,"E7.1.2"),sQuery(id+"F0.wireOp",EDGE,"E7.1.3"),sQuery(id+"F0.wireOp",EDGE,"E7.2.0"),sQuery(id+"F0.wireOp",EDGE,"E7.2.1"),sQuery(id+"F0.wireOp",EDGE,"E7.2.2"),sQuery(id+"F0.wireOp",EDGE,"E7.2.3"),sQuery(id+"F0.wireOp",EDGE,"E7.3.0"),sQuery(id+"F0.wireOp",EDGE,"E7.3.1"),sQuery(id+"F0.wireOp",EDGE,"E7.3.2"),sQuery(id+"F0.wireOp",EDGE,"E7.3.3"),sQuery(id+"F0.wireOp",EDGE,"E7.4.0"),sQuery(id+"F0.wireOp",EDGE,"E7.4.1"),sQuery(id+"F0.wireOp",EDGE,"E7.4.2"),sQuery(id+"F0.wireOp",EDGE,"E7.4.3"),sQuery(id+"F0.wireOp",EDGE,"E7.5.0"),sQuery(id+"F0.wireOp",EDGE,"E7.5.1"),sQuery(id+"F0.wireOp",EDGE,"E7.5.2"),sQuery(id+"F0.wireOp",EDGE,"E7.5.3"),sQuery(id+"F0.wireOp",EDGE,"E7.6.0"),sQuery(id+"F0.wireOp",EDGE,"E7.6.1"),sQuery(id+"F0.wireOp",EDGE,"E7.6.2"),sQuery(id+"F0.wireOp",EDGE,"E7.6.3"),sQuery(id+"F0.wireOp",EDGE,"E7.7.0"),sQuery(id+"F0.wireOp",EDGE,"E7.7.1"),sQuery(id+"F0.wireOp",EDGE,"E7.7.2"),sQuery(id+"F0.wireOp",EDGE,"E7.7.3"),sQuery(id+"F0.wireOp",EDGE,"E7.8.0"),sQuery(id+"F0.wireOp",EDGE,"E7.8.1"),sQuery(id+"F0.wireOp",EDGE,"E7.8.2"),sQuery(id+"F0.wireOp",EDGE,"E7.8.3"),sQuery(id+"F0.wireOp",EDGE,"E7.9.0"),sQuery(id+"F0.wireOp",EDGE,"E7.9.1"),sQuery(id+"F0.wireOp",EDGE,"E7.9.2"),sQuery(id+"F0.wireOp",EDGE,"E7.9.3"),sQuery(id+"F0.wireOp",EDGE,"E7.10.0"),sQuery(id+"F0.wireOp",EDGE,"E7.10.1"),sQuery(id+"F0.wireOp",EDGE,"E7.10.2"),sQuery(id+"F0.wireOp",EDGE,"E7.10.3"),sQuery(id+"F0.wireOp",EDGE,"E7.11.0"),sQuery(id+"F0.wireOp",EDGE,"E7.11.1"),sQuery(id+"F0.wireOp",EDGE,"E7.11.2"),sQuery(id+"F0.wireOp",EDGE,"E7.11.3"),sQuery(id+"F0.wireOp",EDGE,"E7.12.0"),sQuery(id+"F0.wireOp",EDGE,"E7.12.1"),sQuery(id+"F0.wireOp",EDGE,"E7.12.2"),sQuery(id+"F0.wireOp",EDGE,"E7.12.3"),sQuery(id+"F0.wireOp",EDGE,"E7.13.0"),sQuery(id+"F0.wireOp",EDGE,"E7.13.1"),sQuery(id+"F0.wireOp",EDGE,"E7.13.2"),sQuery(id+"F0.wireOp",EDGE,"E7.13.3"),sQuery(id+"F0.wireOp",EDGE,"E7.14.0"),sQuery(id+"F0.wireOp",EDGE,"E7.14.1"),sQuery(id+"F0.wireOp",EDGE,"E7.14.2"),sQuery(id+"F0.wireOp",EDGE,"E7.14.3"),sQuery(id+"F0.wireOp",EDGE,"E7.15.0"),sQuery(id+"F0.wireOp",EDGE,"E7.15.1"),sQuery(id+"F0.wireOp",EDGE,"E7.15.2"),sQuery(id+"F0.wireOp",EDGE,"E7.15.3"),sQuery(id+"F0.wireOp",EDGE,"E7.16.0"),sQuery(id+"F0.wireOp",EDGE,"E7.16.1"),sQuery(id+"F0.wireOp",EDGE,"E7.16.2"),sQuery(id+"F0.wireOp",EDGE,"E7.16.3"),sQuery(id+"F0.wireOp",EDGE,"E7.17.0"),sQuery(id+"F0.wireOp",EDGE,"E7.17.1"),sQuery(id+"F0.wireOp",EDGE,"E7.17.2"),sQuery(id+"F0.wireOp",EDGE,"E7.17.3"),sQuery(id+"F0.wireOp",EDGE,"E7.18.0"),sQuery(id+"F0.wireOp",EDGE,"E7.18.1"),sQuery(id+"F0.wireOp",EDGE,"E7.18.2"),sQuery(id+"F0.wireOp",EDGE,"E7.18.3"),sQuery(id+"F0.wireOp",EDGE,"E7.19.0"),sQuery(id+"F0.wireOp",EDGE,"E7.19.1"),sQuery(id+"F0.wireOp",EDGE,"E7.19.2"),sQuery(id+"F0.wireOp",EDGE,"E7.19.3"),sQuery(id+"F0.wireOp",EDGE,"E7.20.0"),sQuery(id+"F0.wireOp",EDGE,"E7.20.1"),sQuery(id+"F0.wireOp",EDGE,"E7.20.2"),sQuery(id+"F0.wireOp",EDGE,"E7.20.3"),sQuery(id+"F0.wireOp",EDGE,"E7.21.0"),sQuery(id+"F0.wireOp",EDGE,"E7.21.1"),sQuery(id+"F0.wireOp",EDGE,"E7.21.2"),sQuery(id+"F0.wireOp",EDGE,"E7.21.3"),sQuery(id+"F0.wireOp",EDGE,"E7.22.0"),sQuery(id+"F0.wireOp",EDGE,"E7.22.1"),sQuery(id+"F0.wireOp",EDGE,"E7.22.2"),sQuery(id+"F0.wireOp",EDGE,"E7.22.3"),sQuery(id+"F0.wireOp",EDGE,"E7.23.0"),sQuery(id+"F0.wireOp",EDGE,"E7.23.1"),sQuery(id+"F0.wireOp",EDGE,"E7.23.2"),sQuery(id+"F0.wireOp",EDGE,"E7.23.3"),sQuery(id+"F0.wireOp",EDGE,"E7.24.0"),sQuery(id+"F0.wireOp",EDGE,"E7.24.1"),sQuery(id+"F0.wireOp",EDGE,"E7.24.2"),sQuery(id+"F0.wireOp",EDGE,"E7.24.3"),sQuery(id+"F0.wireOp",EDGE,"E7.25.0"),sQuery(id+"F0.wireOp",EDGE,"E7.25.1"),sQuery(id+"F0.wireOp",EDGE,"E7.25.2"),sQuery(id+"F0.wireOp",EDGE,"E7.25.3"),sQuery(id+"F0.wireOp",EDGE,"E7.26.0"),sQuery(id+"F0.wireOp",EDGE,"E7.26.1"),sQuery(id+"F0.wireOp",EDGE,"E7.26.2"),sQuery(id+"F0.wireOp",EDGE,"E7.26.3"),sQuery(id+"F0.wireOp",EDGE,"E7.27.0"),sQuery(id+"F0.wireOp",EDGE,"E7.27.1"),sQuery(id+"F0.wireOp",EDGE,"E7.27.2"),sQuery(id+"F0.wireOp",EDGE,"E7.27.3"),sQuery(id+"F0.wireOp",EDGE,"E7.28.0"),sQuery(id+"F0.wireOp",EDGE,"E7.28.1"),sQuery(id+"F0.wireOp",EDGE,"E7.28.2"),sQuery(id+"F0.wireOp",EDGE,"E7.28.3"),sQuery(id+"F0.wireOp",EDGE,"E7.29.0"),sQuery(id+"F0.wireOp",EDGE,"E7.29.1"),sQuery(id+"F0.wireOp",EDGE,"E7.29.2"),sQuery(id+"F0.wireOp",EDGE,"E7.29.3"),sQuery(id+"F0.wireOp",EDGE,"E7.30.0"),sQuery(id+"F0.wireOp",EDGE,"E7.30.1"),sQuery(id+"F0.wireOp",EDGE,"E7.30.2"),sQuery(id+"F0.wireOp",EDGE,"E7.30.3"),sQuery(id+"F0.wireOp",EDGE,"E7.31.0"),sQuery(id+"F0.wireOp",EDGE,"E7.31.1"),sQuery(id+"F0.wireOp",EDGE,"E7.31.2"),sQuery(id+"F0.wireOp",EDGE,"E7.31.3"),sQuery(id+"F0.wireOp",EDGE,"E7.32.0"),sQuery(id+"F0.wireOp",EDGE,"E7.32.1"),sQuery(id+"F0.wireOp",EDGE,"E7.32.2"),sQuery(id+"F0.wireOp",EDGE,"E7.32.3"),sQuery(id+"F0.wireOp",EDGE,"E7.33.0"),sQuery(id+"F0.wireOp",EDGE,"E7.33.1"),sQuery(id+"F0.wireOp",EDGE,"E7.33.2"),sQuery(id+"F0.wireOp",EDGE,"E7.33.3"),sQuery(id+"F0.wireOp",EDGE,"E7.34.0"),sQuery(id+"F0.wireOp",EDGE,"E7.34.1"),sQuery(id+"F0.wireOp",EDGE,"E7.34.2"),sQuery(id+"F0.wireOp",EDGE,"E7.34.3"),sQuery(id+"F0.wireOp",EDGE,"E7.35.0"),sQuery(id+"F0.wireOp",EDGE,"E7.35.1"),sQuery(id+"F0.wireOp",EDGE,"E7.35.2"),sQuery(id+"F0.wireOp",EDGE,"E7.35.3"),sQuery(id+"F0.wireOp",EDGE,"E7.36.0"),sQuery(id+"F0.wireOp",EDGE,"E7.36.1"),sQuery(id+"F0.wireOp",EDGE,"E7.36.2"),sQuery(id+"F0.wireOp",EDGE,"E7.36.3"),sQuery(id+"F0.wireOp",EDGE,"E7.37.0"),sQuery(id+"F0.wireOp",EDGE,"E7.37.1"),sQuery(id+"F0.wireOp",EDGE,"E7.37.2"),sQuery(id+"F0.wireOp",EDGE,"E7.37.3"),sQuery(id+"F0.wireOp",EDGE,"E7.38.0"),sQuery(id+"F0.wireOp",EDGE,"E7.38.1"),sQuery(id+"F0.wireOp",EDGE,"E7.38.2"),sQuery(id+"F0.wireOp",EDGE,"E7.38.3"),sQuery(id+"F0.wireOp",EDGE,"E7.39.0"),sQuery(id+"F0.wireOp",EDGE,"E7.39.1"),sQuery(id+"F0.wireOp",EDGE,"E7.39.2"),sQuery(id+"F0.wireOp",EDGE,"E7.39.3"),sQuery(id+"F0.wireOp",EDGE,"E8"),sQuery(id+"F0.wireOp",EDGE,"E9"),sQuery(id+"F0.wireOp",EDGE,"E10"),sQuery(id+"F0.wireOp",EDGE,"E12.trimOffspring"),sQuery(id+"F0.wireOp",EDGE,"E13.trimOffspring"),sQuery(id+"F0.wireOp",EDGE,"E14.trimOffspring"),sQuery(id+"F0.wireOp",EDGE,"E15.1.0"),sQuery(id+"F0.wireOp",EDGE,"E15.1.1"),sQuery(id+"F0.wireOp",EDGE,"E15.1.2"),sQuery(id+"F0.wireOp",EDGE,"E15.1.3"),sQuery(id+"F0.wireOp",EDGE,"E15.2.0"),sQuery(id+"F0.wireOp",EDGE,"E15.2.1"),sQuery(id+"F0.wireOp",EDGE,"E15.2.2"),sQuery(id+"F0.wireOp",EDGE,"E15.2.3"),sQuery(id+"F0.wireOp",EDGE,"E15.3.0"),sQuery(id+"F0.wireOp",EDGE,"E15.3.1"),sQuery(id+"F0.wireOp",EDGE,"E15.3.2"),sQuery(id+"F0.wireOp",EDGE,"E15.3.3"),sQuery(id+"F0.wireOp",EDGE,"E15.4.0"),sQuery(id+"F0.wireOp",EDGE,"E15.4.1"),sQuery(id+"F0.wireOp",EDGE,"E15.4.2"),sQuery(id+"F0.wireOp",EDGE,"E15.4.3"),sQuery(id+"F0.wireOp",EDGE,"E15.5.0"),sQuery(id+"F0.wireOp",EDGE,"E15.5.1"),sQuery(id+"F0.wireOp",EDGE,"E15.5.2"),sQuery(id+"F0.wireOp",EDGE,"E15.5.3"),sQuery(id+"F0.wireOp",EDGE,"E15.6.0"),sQuery(id+"F0.wireOp",EDGE,"E15.6.1"),sQuery(id+"F0.wireOp",EDGE,"E15.6.2"),sQuery(id+"F0.wireOp",EDGE,"E15.6.3"),sQuery(id+"F0.wireOp",EDGE,"E15.7.0"),sQuery(id+"F0.wireOp",EDGE,"E15.7.1"),sQuery(id+"F0.wireOp",EDGE,"E15.7.2"),sQuery(id+"F0.wireOp",EDGE,"E15.7.3"),sQuery(id+"F0.wireOp",EDGE,"E15.8.0"),sQuery(id+"F0.wireOp",EDGE,"E15.8.1"),sQuery(id+"F0.wireOp",EDGE,"E15.8.2"),sQuery(id+"F0.wireOp",EDGE,"E15.8.3"),sQuery(id+"F0.wireOp",EDGE,"E15.9.0"),sQuery(id+"F0.wireOp",EDGE,"E15.9.1"),sQuery(id+"F0.wireOp",EDGE,"E15.9.2"),sQuery(id+"F0.wireOp",EDGE,"E15.9.3"),sQuery(id+"F0.wireOp",EDGE,"E15.10.0"),sQuery(id+"F0.wireOp",EDGE,"E15.10.1"),sQuery(id+"F0.wireOp",EDGE,"E15.10.2"),sQuery(id+"F0.wireOp",EDGE,"E15.10.3"),sQuery(id+"F0.wireOp",EDGE,"E15.11.0"),sQuery(id+"F0.wireOp",EDGE,"E15.11.1"),sQuery(id+"F0.wireOp",EDGE,"E15.11.2"),sQuery(id+"F0.wireOp",EDGE,"E15.11.3"),sQuery(id+"F0.wireOp",EDGE,"E16.bottom"),sQuery(id+"F0.wireOp",EDGE,"E16.top"),sQuery(id+"F0.wireOp",EDGE,"E16.left"),sQuery(id+"F0.wireOp",EDGE,"E16.right")])],"isStart":false});
            var sketch = newSketch(context, id + "F5", { "sketchPlane" : qUnion([Q0])});
            skCircle(sketch, "E18", {"center": v(0, 0) * mm, "radius": 150.15 * mm});
            skCircle(sketch, "E19", {"center": v(0, 0) * mm, "radius": 11.5 * mm});
            skSolve(sketch);
        }
        {
            var Q0;
            Q0=qSketchRegion(id+"F5",true);
            extrude(context, id + "F6", {"entities" : qUnion([Q0]), "operationType" : NewBodyOperationType.ADD, "oppositeDirection" : true, "depth" : 5 * mm, "offsetDistance" : 25 * mm});
        }
        {
            var Q0;
            Q0=makeQuery(id+"F6.boolean.opBoolean","MERGE",FACE,{"derivedFrom":[makeQuery(id+"F1.opExtrude","CAP_FACE",FACE,{"disambiguationData":[OSD([sQuery(id+"F0.wireOp",EDGE,"E0"),sQuery(id+"F0.wireOp",EDGE,"E1"),sQuery(id+"F0.wireOp",EDGE,"E6"),sQuery(id+"F0.wireOp",EDGE,"E7.1.0"),sQuery(id+"F0.wireOp",EDGE,"E7.1.1"),sQuery(id+"F0.wireOp",EDGE,"E7.1.2"),sQuery(id+"F0.wireOp",EDGE,"E7.1.3"),sQuery(id+"F0.wireOp",EDGE,"E7.2.0"),sQuery(id+"F0.wireOp",EDGE,"E7.2.1"),sQuery(id+"F0.wireOp",EDGE,"E7.2.2"),sQuery(id+"F0.wireOp",EDGE,"E7.2.3"),sQuery(id+"F0.wireOp",EDGE,"E7.3.0"),sQuery(id+"F0.wireOp",EDGE,"E7.3.1"),sQuery(id+"F0.wireOp",EDGE,"E7.3.2"),sQuery(id+"F0.wireOp",EDGE,"E7.3.3"),sQuery(id+"F0.wireOp",EDGE,"E7.4.0"),sQuery(id+"F0.wireOp",EDGE,"E7.4.1"),sQuery(id+"F0.wireOp",EDGE,"E7.4.2"),sQuery(id+"F0.wireOp",EDGE,"E7.4.3"),sQuery(id+"F0.wireOp",EDGE,"E7.5.0"),sQuery(id+"F0.wireOp",EDGE,"E7.5.1"),sQuery(id+"F0.wireOp",EDGE,"E7.5.2"),sQuery(id+"F0.wireOp",EDGE,"E7.5.3"),sQuery(id+"F0.wireOp",EDGE,"E7.6.0"),sQuery(id+"F0.wireOp",EDGE,"E7.6.1"),sQuery(id+"F0.wireOp",EDGE,"E7.6.2"),sQuery(id+"F0.wireOp",EDGE,"E7.6.3"),sQuery(id+"F0.wireOp",EDGE,"E7.7.0"),sQuery(id+"F0.wireOp",EDGE,"E7.7.1"),sQuery(id+"F0.wireOp",EDGE,"E7.7.2"),sQuery(id+"F0.wireOp",EDGE,"E7.7.3"),sQuery(id+"F0.wireOp",EDGE,"E7.8.0"),sQuery(id+"F0.wireOp",EDGE,"E7.8.1"),sQuery(id+"F0.wireOp",EDGE,"E7.8.2"),sQuery(id+"F0.wireOp",EDGE,"E7.8.3"),sQuery(id+"F0.wireOp",EDGE,"E7.9.0"),sQuery(id+"F0.wireOp",EDGE,"E7.9.1"),sQuery(id+"F0.wireOp",EDGE,"E7.9.2"),sQuery(id+"F0.wireOp",EDGE,"E7.9.3"),sQuery(id+"F0.wireOp",EDGE,"E7.10.0"),sQuery(id+"F0.wireOp",EDGE,"E7.10.1"),sQuery(id+"F0.wireOp",EDGE,"E7.10.2"),sQuery(id+"F0.wireOp",EDGE,"E7.10.3"),sQuery(id+"F0.wireOp",EDGE,"E7.11.0"),sQuery(id+"F0.wireOp",EDGE,"E7.11.1"),sQuery(id+"F0.wireOp",EDGE,"E7.11.2"),sQuery(id+"F0.wireOp",EDGE,"E7.11.3"),sQuery(id+"F0.wireOp",EDGE,"E7.12.0"),sQuery(id+"F0.wireOp",EDGE,"E7.12.1"),sQuery(id+"F0.wireOp",EDGE,"E7.12.2"),sQuery(id+"F0.wireOp",EDGE,"E7.12.3"),sQuery(id+"F0.wireOp",EDGE,"E7.13.0"),sQuery(id+"F0.wireOp",EDGE,"E7.13.1"),sQuery(id+"F0.wireOp",EDGE,"E7.13.2"),sQuery(id+"F0.wireOp",EDGE,"E7.13.3"),sQuery(id+"F0.wireOp",EDGE,"E7.14.0"),sQuery(id+"F0.wireOp",EDGE,"E7.14.1"),sQuery(id+"F0.wireOp",EDGE,"E7.14.2"),sQuery(id+"F0.wireOp",EDGE,"E7.14.3"),sQuery(id+"F0.wireOp",EDGE,"E7.15.0"),sQuery(id+"F0.wireOp",EDGE,"E7.15.1"),sQuery(id+"F0.wireOp",EDGE,"E7.15.2"),sQuery(id+"F0.wireOp",EDGE,"E7.15.3"),sQuery(id+"F0.wireOp",EDGE,"E7.16.0"),sQuery(id+"F0.wireOp",EDGE,"E7.16.1"),sQuery(id+"F0.wireOp",EDGE,"E7.16.2"),sQuery(id+"F0.wireOp",EDGE,"E7.16.3"),sQuery(id+"F0.wireOp",EDGE,"E7.17.0"),sQuery(id+"F0.wireOp",EDGE,"E7.17.1"),sQuery(id+"F0.wireOp",EDGE,"E7.17.2"),sQuery(id+"F0.wireOp",EDGE,"E7.17.3"),sQuery(id+"F0.wireOp",EDGE,"E7.18.0"),sQuery(id+"F0.wireOp",EDGE,"E7.18.1"),sQuery(id+"F0.wireOp",EDGE,"E7.18.2"),sQuery(id+"F0.wireOp",EDGE,"E7.18.3"),sQuery(id+"F0.wireOp",EDGE,"E7.19.0"),sQuery(id+"F0.wireOp",EDGE,"E7.19.1"),sQuery(id+"F0.wireOp",EDGE,"E7.19.2"),sQuery(id+"F0.wireOp",EDGE,"E7.19.3"),sQuery(id+"F0.wireOp",EDGE,"E7.20.0"),sQuery(id+"F0.wireOp",EDGE,"E7.20.1"),sQuery(id+"F0.wireOp",EDGE,"E7.20.2"),sQuery(id+"F0.wireOp",EDGE,"E7.20.3"),sQuery(id+"F0.wireOp",EDGE,"E7.21.0"),sQuery(id+"F0.wireOp",EDGE,"E7.21.1"),sQuery(id+"F0.wireOp",EDGE,"E7.21.2"),sQuery(id+"F0.wireOp",EDGE,"E7.21.3"),sQuery(id+"F0.wireOp",EDGE,"E7.22.0"),sQuery(id+"F0.wireOp",EDGE,"E7.22.1"),sQuery(id+"F0.wireOp",EDGE,"E7.22.2"),sQuery(id+"F0.wireOp",EDGE,"E7.22.3"),sQuery(id+"F0.wireOp",EDGE,"E7.23.0"),sQuery(id+"F0.wireOp",EDGE,"E7.23.1"),sQuery(id+"F0.wireOp",EDGE,"E7.23.2"),sQuery(id+"F0.wireOp",EDGE,"E7.23.3"),sQuery(id+"F0.wireOp",EDGE,"E7.24.0"),sQuery(id+"F0.wireOp",EDGE,"E7.24.1"),sQuery(id+"F0.wireOp",EDGE,"E7.24.2"),sQuery(id+"F0.wireOp",EDGE,"E7.24.3"),sQuery(id+"F0.wireOp",EDGE,"E7.25.0"),sQuery(id+"F0.wireOp",EDGE,"E7.25.1"),sQuery(id+"F0.wireOp",EDGE,"E7.25.2"),sQuery(id+"F0.wireOp",EDGE,"E7.25.3"),sQuery(id+"F0.wireOp",EDGE,"E7.26.0"),sQuery(id+"F0.wireOp",EDGE,"E7.26.1"),sQuery(id+"F0.wireOp",EDGE,"E7.26.2"),sQuery(id+"F0.wireOp",EDGE,"E7.26.3"),sQuery(id+"F0.wireOp",EDGE,"E7.27.0"),sQuery(id+"F0.wireOp",EDGE,"E7.27.1"),sQuery(id+"F0.wireOp",EDGE,"E7.27.2"),sQuery(id+"F0.wireOp",EDGE,"E7.27.3"),sQuery(id+"F0.wireOp",EDGE,"E7.28.0"),sQuery(id+"F0.wireOp",EDGE,"E7.28.1"),sQuery(id+"F0.wireOp",EDGE,"E7.28.2"),sQuery(id+"F0.wireOp",EDGE,"E7.28.3"),sQuery(id+"F0.wireOp",EDGE,"E7.29.0"),sQuery(id+"F0.wireOp",EDGE,"E7.29.1"),sQuery(id+"F0.wireOp",EDGE,"E7.29.2"),sQuery(id+"F0.wireOp",EDGE,"E7.29.3"),sQuery(id+"F0.wireOp",EDGE,"E7.30.0"),sQuery(id+"F0.wireOp",EDGE,"E7.30.1"),sQuery(id+"F0.wireOp",EDGE,"E7.30.2"),sQuery(id+"F0.wireOp",EDGE,"E7.30.3"),sQuery(id+"F0.wireOp",EDGE,"E7.31.0"),sQuery(id+"F0.wireOp",EDGE,"E7.31.1"),sQuery(id+"F0.wireOp",EDGE,"E7.31.2"),sQuery(id+"F0.wireOp",EDGE,"E7.31.3"),sQuery(id+"F0.wireOp",EDGE,"E7.32.0"),sQuery(id+"F0.wireOp",EDGE,"E7.32.1"),sQuery(id+"F0.wireOp",EDGE,"E7.32.2"),sQuery(id+"F0.wireOp",EDGE,"E7.32.3"),sQuery(id+"F0.wireOp",EDGE,"E7.33.0"),sQuery(id+"F0.wireOp",EDGE,"E7.33.1"),sQuery(id+"F0.wireOp",EDGE,"E7.33.2"),sQuery(id+"F0.wireOp",EDGE,"E7.33.3"),sQuery(id+"F0.wireOp",EDGE,"E7.34.0"),sQuery(id+"F0.wireOp",EDGE,"E7.34.1"),sQuery(id+"F0.wireOp",EDGE,"E7.34.2"),sQuery(id+"F0.wireOp",EDGE,"E7.34.3"),sQuery(id+"F0.wireOp",EDGE,"E7.35.0"),sQuery(id+"F0.wireOp",EDGE,"E7.35.1"),sQuery(id+"F0.wireOp",EDGE,"E7.35.2"),sQuery(id+"F0.wireOp",EDGE,"E7.35.3"),sQuery(id+"F0.wireOp",EDGE,"E7.36.0"),sQuery(id+"F0.wireOp",EDGE,"E7.36.1"),sQuery(id+"F0.wireOp",EDGE,"E7.36.2"),sQuery(id+"F0.wireOp",EDGE,"E7.36.3"),sQuery(id+"F0.wireOp",EDGE,"E7.37.0"),sQuery(id+"F0.wireOp",EDGE,"E7.37.1"),sQuery(id+"F0.wireOp",EDGE,"E7.37.2"),sQuery(id+"F0.wireOp",EDGE,"E7.37.3"),sQuery(id+"F0.wireOp",EDGE,"E7.38.0"),sQuery(id+"F0.wireOp",EDGE,"E7.38.1"),sQuery(id+"F0.wireOp",EDGE,"E7.38.2"),sQuery(id+"F0.wireOp",EDGE,"E7.38.3"),sQuery(id+"F0.wireOp",EDGE,"E7.39.0"),sQuery(id+"F0.wireOp",EDGE,"E7.39.1"),sQuery(id+"F0.wireOp",EDGE,"E7.39.2"),sQuery(id+"F0.wireOp",EDGE,"E7.39.3"),sQuery(id+"F0.wireOp",EDGE,"E8"),sQuery(id+"F0.wireOp",EDGE,"E9"),sQuery(id+"F0.wireOp",EDGE,"E10"),sQuery(id+"F0.wireOp",EDGE,"E12.trimOffspring"),sQuery(id+"F0.wireOp",EDGE,"E13.trimOffspring"),sQuery(id+"F0.wireOp",EDGE,"E14.trimOffspring"),sQuery(id+"F0.wireOp",EDGE,"E15.1.0"),sQuery(id+"F0.wireOp",EDGE,"E15.1.1"),sQuery(id+"F0.wireOp",EDGE,"E15.1.2"),sQuery(id+"F0.wireOp",EDGE,"E15.1.3"),sQuery(id+"F0.wireOp",EDGE,"E15.2.0"),sQuery(id+"F0.wireOp",EDGE,"E15.2.1"),sQuery(id+"F0.wireOp",EDGE,"E15.2.2"),sQuery(id+"F0.wireOp",EDGE,"E15.2.3"),sQuery(id+"F0.wireOp",EDGE,"E15.3.0"),sQuery(id+"F0.wireOp",EDGE,"E15.3.1"),sQuery(id+"F0.wireOp",EDGE,"E15.3.2"),sQuery(id+"F0.wireOp",EDGE,"E15.3.3"),sQuery(id+"F0.wireOp",EDGE,"E15.4.0"),sQuery(id+"F0.wireOp",EDGE,"E15.4.1"),sQuery(id+"F0.wireOp",EDGE,"E15.4.2"),sQuery(id+"F0.wireOp",EDGE,"E15.4.3"),sQuery(id+"F0.wireOp",EDGE,"E15.5.0"),sQuery(id+"F0.wireOp",EDGE,"E15.5.1"),sQuery(id+"F0.wireOp",EDGE,"E15.5.2"),sQuery(id+"F0.wireOp",EDGE,"E15.5.3"),sQuery(id+"F0.wireOp",EDGE,"E15.6.0"),sQuery(id+"F0.wireOp",EDGE,"E15.6.1"),sQuery(id+"F0.wireOp",EDGE,"E15.6.2"),sQuery(id+"F0.wireOp",EDGE,"E15.6.3"),sQuery(id+"F0.wireOp",EDGE,"E15.7.0"),sQuery(id+"F0.wireOp",EDGE,"E15.7.1"),sQuery(id+"F0.wireOp",EDGE,"E15.7.2"),sQuery(id+"F0.wireOp",EDGE,"E15.7.3"),sQuery(id+"F0.wireOp",EDGE,"E15.8.0"),sQuery(id+"F0.wireOp",EDGE,"E15.8.1"),sQuery(id+"F0.wireOp",EDGE,"E15.8.2"),sQuery(id+"F0.wireOp",EDGE,"E15.8.3"),sQuery(id+"F0.wireOp",EDGE,"E15.9.0"),sQuery(id+"F0.wireOp",EDGE,"E15.9.1"),sQuery(id+"F0.wireOp",EDGE,"E15.9.2"),sQuery(id+"F0.wireOp",EDGE,"E15.9.3"),sQuery(id+"F0.wireOp",EDGE,"E15.10.0"),sQuery(id+"F0.wireOp",EDGE,"E15.10.1"),sQuery(id+"F0.wireOp",EDGE,"E15.10.2"),sQuery(id+"F0.wireOp",EDGE,"E15.10.3"),sQuery(id+"F0.wireOp",EDGE,"E15.11.0"),sQuery(id+"F0.wireOp",EDGE,"E15.11.1"),sQuery(id+"F0.wireOp",EDGE,"E15.11.2"),sQuery(id+"F0.wireOp",EDGE,"E15.11.3"),sQuery(id+"F0.wireOp",EDGE,"E16.bottom"),sQuery(id+"F0.wireOp",EDGE,"E16.top"),sQuery(id+"F0.wireOp",EDGE,"E16.left"),sQuery(id+"F0.wireOp",EDGE,"E16.right")])],"isStart":false}),makeQuery(id+"F6.opExtrude","CAP_FACE",FACE,{"disambiguationData":[OSD([sQuery(id+"F5.wireOp",EDGE,"E18"),sQuery(id+"F5.wireOp",EDGE,"E19")])],"isStart":true})]});
            var sketch = newSketch(context, id + "F7", { "sketchPlane" : qUnion([Q0])});
            skCircle(sketch, "E20", {"center": v(0, 0) * mm, "radius": 40 * mm});
            skCircle(sketch, "E21", {"center": v(0, 0) * mm, "radius": 17.5 * mm});
            skSolve(sketch);
        }
        {
            var Q0;
            Q0=qSketchRegion(id+"F7",true);
            extrude(context, id + "F8", {"entities" : qUnion([Q0]), "depth" : 5 * mm, "offsetDistance" : 25 * mm});
        }
        {
            var Q0;
            Q0=makeQuery(id+"F1.opExtrude","SWEPT_BODY",BODY,{"disambiguationData":[OSD([sQuery(id+"F0.wireOp",EDGE,"E0"),sQuery(id+"F0.wireOp",EDGE,"E1"),sQuery(id+"F0.wireOp",EDGE,"E6"),sQuery(id+"F0.wireOp",EDGE,"E7.1.0"),sQuery(id+"F0.wireOp",EDGE,"E7.1.1"),sQuery(id+"F0.wireOp",EDGE,"E7.1.2"),sQuery(id+"F0.wireOp",EDGE,"E7.1.3"),sQuery(id+"F0.wireOp",EDGE,"E7.2.0"),sQuery(id+"F0.wireOp",EDGE,"E7.2.1"),sQuery(id+"F0.wireOp",EDGE,"E7.2.2"),sQuery(id+"F0.wireOp",EDGE,"E7.2.3"),sQuery(id+"F0.wireOp",EDGE,"E7.3.0"),sQuery(id+"F0.wireOp",EDGE,"E7.3.1"),sQuery(id+"F0.wireOp",EDGE,"E7.3.2"),sQuery(id+"F0.wireOp",EDGE,"E7.3.3"),sQuery(id+"F0.wireOp",EDGE,"E7.4.0"),sQuery(id+"F0.wireOp",EDGE,"E7.4.1"),sQuery(id+"F0.wireOp",EDGE,"E7.4.2"),sQuery(id+"F0.wireOp",EDGE,"E7.4.3"),sQuery(id+"F0.wireOp",EDGE,"E7.5.0"),sQuery(id+"F0.wireOp",EDGE,"E7.5.1"),sQuery(id+"F0.wireOp",EDGE,"E7.5.2"),sQuery(id+"F0.wireOp",EDGE,"E7.5.3"),sQuery(id+"F0.wireOp",EDGE,"E7.6.0"),sQuery(id+"F0.wireOp",EDGE,"E7.6.1"),sQuery(id+"F0.wireOp",EDGE,"E7.6.2"),sQuery(id+"F0.wireOp",EDGE,"E7.6.3"),sQuery(id+"F0.wireOp",EDGE,"E7.7.0"),sQuery(id+"F0.wireOp",EDGE,"E7.7.1"),sQuery(id+"F0.wireOp",EDGE,"E7.7.2"),sQuery(id+"F0.wireOp",EDGE,"E7.7.3"),sQuery(id+"F0.wireOp",EDGE,"E7.8.0"),sQuery(id+"F0.wireOp",EDGE,"E7.8.1"),sQuery(id+"F0.wireOp",EDGE,"E7.8.2"),sQuery(id+"F0.wireOp",EDGE,"E7.8.3"),sQuery(id+"F0.wireOp",EDGE,"E7.9.0"),sQuery(id+"F0.wireOp",EDGE,"E7.9.1"),sQuery(id+"F0.wireOp",EDGE,"E7.9.2"),sQuery(id+"F0.wireOp",EDGE,"E7.9.3"),sQuery(id+"F0.wireOp",EDGE,"E7.10.0"),sQuery(id+"F0.wireOp",EDGE,"E7.10.1"),sQuery(id+"F0.wireOp",EDGE,"E7.10.2"),sQuery(id+"F0.wireOp",EDGE,"E7.10.3"),sQuery(id+"F0.wireOp",EDGE,"E7.11.0"),sQuery(id+"F0.wireOp",EDGE,"E7.11.1"),sQuery(id+"F0.wireOp",EDGE,"E7.11.2"),sQuery(id+"F0.wireOp",EDGE,"E7.11.3"),sQuery(id+"F0.wireOp",EDGE,"E7.12.0"),sQuery(id+"F0.wireOp",EDGE,"E7.12.1"),sQuery(id+"F0.wireOp",EDGE,"E7.12.2"),sQuery(id+"F0.wireOp",EDGE,"E7.12.3"),sQuery(id+"F0.wireOp",EDGE,"E7.13.0"),sQuery(id+"F0.wireOp",EDGE,"E7.13.1"),sQuery(id+"F0.wireOp",EDGE,"E7.13.2"),sQuery(id+"F0.wireOp",EDGE,"E7.13.3"),sQuery(id+"F0.wireOp",EDGE,"E7.14.0"),sQuery(id+"F0.wireOp",EDGE,"E7.14.1"),sQuery(id+"F0.wireOp",EDGE,"E7.14.2"),sQuery(id+"F0.wireOp",EDGE,"E7.14.3"),sQuery(id+"F0.wireOp",EDGE,"E7.15.0"),sQuery(id+"F0.wireOp",EDGE,"E7.15.1"),sQuery(id+"F0.wireOp",EDGE,"E7.15.2"),sQuery(id+"F0.wireOp",EDGE,"E7.15.3"),sQuery(id+"F0.wireOp",EDGE,"E7.16.0"),sQuery(id+"F0.wireOp",EDGE,"E7.16.1"),sQuery(id+"F0.wireOp",EDGE,"E7.16.2"),sQuery(id+"F0.wireOp",EDGE,"E7.16.3"),sQuery(id+"F0.wireOp",EDGE,"E7.17.0"),sQuery(id+"F0.wireOp",EDGE,"E7.17.1"),sQuery(id+"F0.wireOp",EDGE,"E7.17.2"),sQuery(id+"F0.wireOp",EDGE,"E7.17.3"),sQuery(id+"F0.wireOp",EDGE,"E7.18.0"),sQuery(id+"F0.wireOp",EDGE,"E7.18.1"),sQuery(id+"F0.wireOp",EDGE,"E7.18.2"),sQuery(id+"F0.wireOp",EDGE,"E7.18.3"),sQuery(id+"F0.wireOp",EDGE,"E7.19.0"),sQuery(id+"F0.wireOp",EDGE,"E7.19.1"),sQuery(id+"F0.wireOp",EDGE,"E7.19.2"),sQuery(id+"F0.wireOp",EDGE,"E7.19.3"),sQuery(id+"F0.wireOp",EDGE,"E7.20.0"),sQuery(id+"F0.wireOp",EDGE,"E7.20.1"),sQuery(id+"F0.wireOp",EDGE,"E7.20.2"),sQuery(id+"F0.wireOp",EDGE,"E7.20.3"),sQuery(id+"F0.wireOp",EDGE,"E7.21.0"),sQuery(id+"F0.wireOp",EDGE,"E7.21.1"),sQuery(id+"F0.wireOp",EDGE,"E7.21.2"),sQuery(id+"F0.wireOp",EDGE,"E7.21.3"),sQuery(id+"F0.wireOp",EDGE,"E7.22.0"),sQuery(id+"F0.wireOp",EDGE,"E7.22.1"),sQuery(id+"F0.wireOp",EDGE,"E7.22.2"),sQuery(id+"F0.wireOp",EDGE,"E7.22.3"),sQuery(id+"F0.wireOp",EDGE,"E7.23.0"),sQuery(id+"F0.wireOp",EDGE,"E7.23.1"),sQuery(id+"F0.wireOp",EDGE,"E7.23.2"),sQuery(id+"F0.wireOp",EDGE,"E7.23.3"),sQuery(id+"F0.wireOp",EDGE,"E7.24.0"),sQuery(id+"F0.wireOp",EDGE,"E7.24.1"),sQuery(id+"F0.wireOp",EDGE,"E7.24.2"),sQuery(id+"F0.wireOp",EDGE,"E7.24.3"),sQuery(id+"F0.wireOp",EDGE,"E7.25.0"),sQuery(id+"F0.wireOp",EDGE,"E7.25.1"),sQuery(id+"F0.wireOp",EDGE,"E7.25.2"),sQuery(id+"F0.wireOp",EDGE,"E7.25.3"),sQuery(id+"F0.wireOp",EDGE,"E7.26.0"),sQuery(id+"F0.wireOp",EDGE,"E7.26.1"),sQuery(id+"F0.wireOp",EDGE,"E7.26.2"),sQuery(id+"F0.wireOp",EDGE,"E7.26.3"),sQuery(id+"F0.wireOp",EDGE,"E7.27.0"),sQuery(id+"F0.wireOp",EDGE,"E7.27.1"),sQuery(id+"F0.wireOp",EDGE,"E7.27.2"),sQuery(id+"F0.wireOp",EDGE,"E7.27.3"),sQuery(id+"F0.wireOp",EDGE,"E7.28.0"),sQuery(id+"F0.wireOp",EDGE,"E7.28.1"),sQuery(id+"F0.wireOp",EDGE,"E7.28.2"),sQuery(id+"F0.wireOp",EDGE,"E7.28.3"),sQuery(id+"F0.wireOp",EDGE,"E7.29.0"),sQuery(id+"F0.wireOp",EDGE,"E7.29.1"),sQuery(id+"F0.wireOp",EDGE,"E7.29.2"),sQuery(id+"F0.wireOp",EDGE,"E7.29.3"),sQuery(id+"F0.wireOp",EDGE,"E7.30.0"),sQuery(id+"F0.wireOp",EDGE,"E7.30.1"),sQuery(id+"F0.wireOp",EDGE,"E7.30.2"),sQuery(id+"F0.wireOp",EDGE,"E7.30.3"),sQuery(id+"F0.wireOp",EDGE,"E7.31.0"),sQuery(id+"F0.wireOp",EDGE,"E7.31.1"),sQuery(id+"F0.wireOp",EDGE,"E7.31.2"),sQuery(id+"F0.wireOp",EDGE,"E7.31.3"),sQuery(id+"F0.wireOp",EDGE,"E7.32.0"),sQuery(id+"F0.wireOp",EDGE,"E7.32.1"),sQuery(id+"F0.wireOp",EDGE,"E7.32.2"),sQuery(id+"F0.wireOp",EDGE,"E7.32.3"),sQuery(id+"F0.wireOp",EDGE,"E7.33.0"),sQuery(id+"F0.wireOp",EDGE,"E7.33.1"),sQuery(id+"F0.wireOp",EDGE,"E7.33.2"),sQuery(id+"F0.wireOp",EDGE,"E7.33.3"),sQuery(id+"F0.wireOp",EDGE,"E7.34.0"),sQuery(id+"F0.wireOp",EDGE,"E7.34.1"),sQuery(id+"F0.wireOp",EDGE,"E7.34.2"),sQuery(id+"F0.wireOp",EDGE,"E7.34.3"),sQuery(id+"F0.wireOp",EDGE,"E7.35.0"),sQuery(id+"F0.wireOp",EDGE,"E7.35.1"),sQuery(id+"F0.wireOp",EDGE,"E7.35.2"),sQuery(id+"F0.wireOp",EDGE,"E7.35.3"),sQuery(id+"F0.wireOp",EDGE,"E7.36.0"),sQuery(id+"F0.wireOp",EDGE,"E7.36.1"),sQuery(id+"F0.wireOp",EDGE,"E7.36.2"),sQuery(id+"F0.wireOp",EDGE,"E7.36.3"),sQuery(id+"F0.wireOp",EDGE,"E7.37.0"),sQuery(id+"F0.wireOp",EDGE,"E7.37.1"),sQuery(id+"F0.wireOp",EDGE,"E7.37.2"),sQuery(id+"F0.wireOp",EDGE,"E7.37.3"),sQuery(id+"F0.wireOp",EDGE,"E7.38.0"),sQuery(id+"F0.wireOp",EDGE,"E7.38.1"),sQuery(id+"F0.wireOp",EDGE,"E7.38.2"),sQuery(id+"F0.wireOp",EDGE,"E7.38.3"),sQuery(id+"F0.wireOp",EDGE,"E7.39.0"),sQuery(id+"F0.wireOp",EDGE,"E7.39.1"),sQuery(id+"F0.wireOp",EDGE,"E7.39.2"),sQuery(id+"F0.wireOp",EDGE,"E7.39.3"),sQuery(id+"F0.wireOp",EDGE,"E8"),sQuery(id+"F0.wireOp",EDGE,"E9"),sQuery(id+"F0.wireOp",EDGE,"E10"),sQuery(id+"F0.wireOp",EDGE,"E12.trimOffspring"),sQuery(id+"F0.wireOp",EDGE,"E13.trimOffspring"),sQuery(id+"F0.wireOp",EDGE,"E14.trimOffspring"),sQuery(id+"F0.wireOp",EDGE,"E15.1.0"),sQuery(id+"F0.wireOp",EDGE,"E15.1.1"),sQuery(id+"F0.wireOp",EDGE,"E15.1.2"),sQuery(id+"F0.wireOp",EDGE,"E15.1.3"),sQuery(id+"F0.wireOp",EDGE,"E15.2.0"),sQuery(id+"F0.wireOp",EDGE,"E15.2.1"),sQuery(id+"F0.wireOp",EDGE,"E15.2.2"),sQuery(id+"F0.wireOp",EDGE,"E15.2.3"),sQuery(id+"F0.wireOp",EDGE,"E15.3.0"),sQuery(id+"F0.wireOp",EDGE,"E15.3.1"),sQuery(id+"F0.wireOp",EDGE,"E15.3.2"),sQuery(id+"F0.wireOp",EDGE,"E15.3.3"),sQuery(id+"F0.wireOp",EDGE,"E15.4.0"),sQuery(id+"F0.wireOp",EDGE,"E15.4.1"),sQuery(id+"F0.wireOp",EDGE,"E15.4.2"),sQuery(id+"F0.wireOp",EDGE,"E15.4.3"),sQuery(id+"F0.wireOp",EDGE,"E15.5.0"),sQuery(id+"F0.wireOp",EDGE,"E15.5.1"),sQuery(id+"F0.wireOp",EDGE,"E15.5.2"),sQuery(id+"F0.wireOp",EDGE,"E15.5.3"),sQuery(id+"F0.wireOp",EDGE,"E15.6.0"),sQuery(id+"F0.wireOp",EDGE,"E15.6.1"),sQuery(id+"F0.wireOp",EDGE,"E15.6.2"),sQuery(id+"F0.wireOp",EDGE,"E15.6.3"),sQuery(id+"F0.wireOp",EDGE,"E15.7.0"),sQuery(id+"F0.wireOp",EDGE,"E15.7.1"),sQuery(id+"F0.wireOp",EDGE,"E15.7.2"),sQuery(id+"F0.wireOp",EDGE,"E15.7.3"),sQuery(id+"F0.wireOp",EDGE,"E15.8.0"),sQuery(id+"F0.wireOp",EDGE,"E15.8.1"),sQuery(id+"F0.wireOp",EDGE,"E15.8.2"),sQuery(id+"F0.wireOp",EDGE,"E15.8.3"),sQuery(id+"F0.wireOp",EDGE,"E15.9.0"),sQuery(id+"F0.wireOp",EDGE,"E15.9.1"),sQuery(id+"F0.wireOp",EDGE,"E15.9.2"),sQuery(id+"F0.wireOp",EDGE,"E15.9.3"),sQuery(id+"F0.wireOp",EDGE,"E15.10.0"),sQuery(id+"F0.wireOp",EDGE,"E15.10.1"),sQuery(id+"F0.wireOp",EDGE,"E15.10.2"),sQuery(id+"F0.wireOp",EDGE,"E15.10.3"),sQuery(id+"F0.wireOp",EDGE,"E15.11.0"),sQuery(id+"F0.wireOp",EDGE,"E15.11.1"),sQuery(id+"F0.wireOp",EDGE,"E15.11.2"),sQuery(id+"F0.wireOp",EDGE,"E15.11.3"),sQuery(id+"F0.wireOp",EDGE,"E16.bottom"),sQuery(id+"F0.wireOp",EDGE,"E16.top"),sQuery(id+"F0.wireOp",EDGE,"E16.left"),sQuery(id+"F0.wireOp",EDGE,"E16.right")])]});
            deleteBodies(context, id + "F9", {"entities" : qUnion([Q0])});
        }
        {
            var Q0;
            Q0=makeQuery(id+"F4.opExtrude","SWEPT_BODY",BODY,{"disambiguationData":[OSD([sQuery(id+"F2.wireOp",EDGE,"E17")])]});
            deleteBodies(context, id + "F10", {"entities" : qUnion([Q0])});
        }
    });
